# Revit family: d0088071_REVIT-TP
name_source: partatom
category: Mechanical Equipment
revit_build: Autodesk Revit 2017 (Build: 20190507_1515(x64)
units: mm (PartAtom-declared; Revit-internal decimal feet)

## family parameters
Always vertical = Yes
Cut with Voids When Loaded = No
Part Type = Normal
Room Calculation Point = No
Round Connector Dimension = Use Radius
Shared = No
Work Plane-Based = No

## types (58) — shared parameters
250 GT Visibility = No
3500 4000 GT Visibility = No
500 3000 GT Visibility = Yes
Aquaplex = Yes
Assembly Code = D3040400
Blower Motor HP = 0.33333
Description = PVI Turbopower - Water Heater
Disclaimer = This rendering is for building modeling purposes only. Submittal/catalog is still the contract document. PVI reserves the right to change design and specification without notice.
Drain Angle = 0.00°
Enclosure Height = 16"
Enclosure Width = 9"
Energy Radius = 14 1/2"
Flue Collector Radius = 11 1/4"
Flue Extension = 18 1/4"
Manufacturer = PVI Industries, LLC
Relief Valve NPT = 1"
Relief Valve Radius = 1/2"
URL = www.pvi.com

## per-type parameters (varying)
- 2500 L 1500 A-TP: 500-3000 GIY=5 7/8"; A=13 3/4"; Air Inlet Depth=7"; Air Inlet Diameter=8"; Air Inlet Extension=20 15/16"; Air Inlet Radius=4"; Air Inlet Width=9"; Air Inlet X=15 15/16"; Air Inlet Y=7 3/16"; Air Inlet Y Offset=2 11/16"; Air Inlet Z Offset=5 3/8"; B=4"; Burner Depth=25 15/16"; Burner Height=16 5/8"; Burner Width=22 1/4"; Clearance Front=114 1/2"; Clearance Rear=55 1/2"; Clearance Sides=55 1/2"; Cold Water Extension=38 1/2"; Cold Water NPT=3"; Cold Water Radius=1 1/2"; Control Panel Extension=44 1/2"; Current=2 A; Drain Extension=41 3/8"; Drain NPT=1 1/2"; Drain Radius=3/4"; Energy Extension=49 1/16"; FC OAL=64 9/16"; Flat Side Distance=75"; Flue Collector Extension=15 1/2"; Flue Diameter=10"; Flue Location=56 13/16"; Flue Radius=5"; Front Skid Extension=112 1/2"; GT Conn Z=104 15/16"; GT Z=66 9/16"; Gas Conn X=44 1/8"; Gas Conn Y=15 7/8"; Gas Inlet NPT=2 1/2"; Gas Inlet Radius=1 1/4"; Gas Inlet X=24 1/8"; Gas Inlet Y=5 7/8"; Gas Inlet Z=40 3/8"; Height to Cold Inlet=21 1/4"; Height to Drain=2 1/4"; Height to Energy=32 3/8"; Height to Hot Outlet=84 1/2"; Height to Hot Outlet Actual=84 1/2"; Height to Relief=85 1/8"; Height to Relief Actual=85 1/8"; Hot Outlet Angle=90.00°; Hot Water Extension=38 1/2"; Hot Water NPT=3"; Hot Water Radius=1 1/2"; Input Btu/h=2010000; Nominal Storage=1500 gal; Rear Access Extension=-45 1/2"; Rear Skid Extension=37 1/2"; Recovery Rate 40F to 140F (gph)=2000; Relief Extension=40 1/2"; Size=1500; Skid Center Dist=21 1/2"; Skid Length=75"; Skid Spacing=43"; Unit Height=104 1/2"; Unit Height Actual=104 1/2"; Unit Radius=37 1/2"; Weight=4540
- 2000 L 1500 A-TP: 500-3000 GIY=5 1/2"; A=13 3/4"; Air Inlet Depth=7"; Air Inlet Diameter=8"; Air Inlet Extension=20 15/16"; Air Inlet Radius=4"; Air Inlet Width=9"; Air Inlet X=15 15/16"; Air Inlet Y=7 3/16"; Air Inlet Y Offset=2 11/16"; Air Inlet Z Offset=5 3/8"; B=4"; Burner Depth=25 15/16"; Burner Height=16 5/8"; Burner Width=22 1/4"; Clearance Front=114 1/2"; Clearance Rear=55 1/2"; Clearance Sides=55 1/2"; Cold Water Extension=38 1/2"; Cold Water NPT=3"; Cold Water Radius=1 1/2"; Control Panel Extension=44 1/2"; Current=2 A; Drain Extension=41 3/8"; Drain NPT=1 1/2"; Drain Radius=3/4"; Energy Extension=49 1/16"; FC OAL=64 9/16"; Flat Side Distance=75"; Flue Collector Extension=15 1/2"; Flue Diameter=10"; Flue Location=56 13/16"; Flue Radius=5"; Front Skid Extension=112 1/2"; GT Conn Z=100 5/8"; GT Z=66 9/16"; Gas Conn X=42"; Gas Conn Y=15 1/2"; Gas Inlet NPT=2"; Gas Inlet Radius=1"; Gas Inlet X=22"; Gas Inlet Y=5 1/2"; Gas Inlet Z=36 1/16"; Height to Cold Inlet=21 1/4"; Height to Drain=2 1/4"; Height to Energy=32 3/8"; Height to Hot Outlet=84 1/2"; Height to Hot Outlet Actual=84 1/2"; Height to Relief=85 1/8"; Height to Relief Actual=85 1/8"; Hot Outlet Angle=90.00°; Hot Water Extension=38 1/2"; Hot Water NPT=3"; Hot Water Radius=1 1/2"; Input Btu/h=1600000; Nominal Storage=1500 gal; Rear Access Extension=-45 1/2"; Rear Skid Extension=37 1/2"; Recovery Rate 40F to 140F (gph)=1600; Relief Extension=40 1/2"; Size=1500; Skid Center Dist=21 1/2"; Skid Length=75"; Skid Spacing=43"; Unit Height=104 1/2"; Unit Height Actual=104 1/2"; Unit Radius=37 1/2"; Weight=4520
- 1500 L 1500 A-TP: 500-3000 GIY=5 1/2"; A=8 3/8"; Air Inlet Depth=3 1/8"; Air Inlet Diameter=6"; Air Inlet Extension=18 15/16"; Air Inlet Radius=3"; Air Inlet Width=6 3/8"; Air Inlet X=14 7/8"; Air Inlet Y=5 1/4"; Air Inlet Y Offset=2 1/16"; Air Inlet Z Offset=2 1/16"; B=3 15/16"; Burner Depth=15 1/2"; Burner Height=13 3/4"; Burner Width=14 11/16"; Clearance Front=99 1/2"; Clearance Rear=55 1/2"; Clearance Sides=55 1/2"; Cold Water Extension=38 1/2"; Cold Water NPT=3"; Cold Water Radius=1 1/2"; Control Panel Extension=44 1/2"; Current=2 A; Drain Extension=41 3/8"; Drain NPT=1 1/2"; Drain Radius=3/4"; Energy Extension=44 1/2"; FC OAL=60"; Flat Side Distance=75"; Flue Collector Extension=15 1/2"; Flue Diameter=8"; Flue Location=52 1/4"; Flue Radius=4"; Front Skid Extension=112 1/2"; GT Conn Z=96 7/16"; GT Z=62"; Gas Conn X=40 1/2"; Gas Conn Y=15 1/2"; Gas Inlet NPT=2"; Gas Inlet Radius=1"; Gas Inlet X=20 1/2"; Gas Inlet Y=5 1/2"; Gas Inlet Z=36 7/16"; Height to Cold Inlet=21 1/4"; Height to Drain=2 1/4"; Height to Energy=32 3/8"; Height to Hot Outlet=84 1/2"; Height to Hot Outlet Actual=84 1/2"; Height to Relief=85 1/8"; Height to Relief Actual=85 1/8"; Hot Outlet Angle=90.00°; Hot Water Extension=38 1/2"; Hot Water NPT=3"; Hot Water Radius=1 1/2"; Input Btu/h=1200000; Nominal Storage=1500 gal; Rear Access Extension=0"; Rear Skid Extension=37 1/2"; Recovery Rate 40F to 140F (gph)=1200; Relief Extension=40 1/2"; Size=1500; Skid Center Dist=21 1/2"; Skid Length=75"; Skid Spacing=43"; Unit Height=104 1/2"; Unit Height Actual=104 1/2"; Unit Radius=37 1/2"; Weight=4085
- 1250 L 1500 A-TP: 500-3000 GIY=5 1/2"; A=8 3/8"; Air Inlet Depth=3 1/8"; Air Inlet Diameter=6"; Air Inlet Extension=18 15/16"; Air Inlet Radius=3"; Air Inlet Width=6 3/8"; Air Inlet X=14 7/8"; Air Inlet Y=5 1/4"; Air Inlet Y Offset=2 1/16"; Air Inlet Z Offset=2 1/16"; B=3 15/16"; Burner Depth=15 1/2"; Burner Height=13 3/4"; Burner Width=14 11/16"; Clearance Front=99 1/2"; Clearance Rear=55 1/2"; Clearance Sides=55 1/2"; Cold Water Extension=38 1/2"; Cold Water NPT=3"; Cold Water Radius=1 1/2"; Control Panel Extension=44 1/2"; Current=2 A; Drain Extension=41 3/8"; Drain NPT=1 1/2"; Drain Radius=3/4"; Energy Extension=44 1/2"; FC OAL=60"; Flat Side Distance=75"; Flue Collector Extension=15 1/2"; Flue Diameter=8"; Flue Location=52 1/4"; Flue Radius=4"; Front Skid Extension=112 1/2"; GT Conn Z=96 7/16"; GT Z=62"; Gas Conn X=40 1/2"; Gas Conn Y=15 1/2"; Gas Inlet NPT=2"; Gas Inlet Radius=1"; Gas Inlet X=20 1/2"; Gas Inlet Y=5 1/2"; Gas Inlet Z=36 7/16"; Height to Cold Inlet=21 1/4"; Height to Drain=2 1/4"; Height to Energy=32 3/8"; Height to Hot Outlet=84 1/2"; Height to Hot Outlet Actual=84 1/2"; Height to Relief=85 1/8"; Height to Relief Actual=85 1/8"; Hot Outlet Angle=90.00°; Hot Water Extension=38 1/2"; Hot Water NPT=3"; Hot Water Radius=1 1/2"; Input Btu/h=1000000; Nominal Storage=1500 gal; Rear Access Extension=0"; Rear Skid Extension=37 1/2"; Recovery Rate 40F to 140F (gph)=1000; Relief Extension=40 1/2"; Size=1500; Skid Center Dist=21 1/2"; Skid Length=75"; Skid Spacing=43"; Unit Height=104 1/2"; Unit Height Actual=104 1/2"; Unit Radius=37 1/2"; Weight=4075
- 1000 L 1500 A-TP: 500-3000 GIY=4 1/2"; A=8 3/8"; Air Inlet Depth=3 1/8"; Air Inlet Diameter=6"; Air Inlet Extension=18 15/16"; Air Inlet Radius=3"; Air Inlet Width=6 3/8"; Air Inlet X=14 7/8"; Air Inlet Y=5 1/4"; Air Inlet Y Offset=2 1/16"; Air Inlet Z Offset=2 1/16"; B=3 15/16"; Burner Depth=15 1/2"; Burner Height=13 3/4"; Burner Width=14 11/16"; Clearance Front=91 1/2"; Clearance Rear=55 1/2"; Clearance Sides=55 1/2"; Cold Water Extension=38 1/2"; Cold Water NPT=3"; Cold Water Radius=1 1/2"; Control Panel Extension=44 1/2"; Current=2 A; Drain Extension=41 3/8"; Drain NPT=1 1/2"; Drain Radius=3/4"; Energy Extension=43 3/4"; FC OAL=52"; Flat Side Distance=75"; Flue Collector Extension=8 1/4"; Flue Diameter=8"; Flue Location=47 7/8"; Flue Radius=4"; Front Skid Extension=112 1/2"; GT Conn Z=79 11/16"; GT Z=54"; Gas Conn X=40 1/2"; Gas Conn Y=14 1/2"; Gas Inlet NPT=1 1/4"; Gas Inlet Radius=5/8"; Gas Inlet X=20 1/2"; Gas Inlet Y=4 1/2"; Gas Inlet Z=27 11/16"; Height to Cold Inlet=21 1/4"; Height to Drain=2 1/4"; Height to Energy=32 3/8"; Height to Hot Outlet=84 1/2"; Height to Hot Outlet Actual=84 1/2"; Height to Relief=85 1/8"; Height to Relief Actual=85 1/8"; Hot Outlet Angle=90.00°; Hot Water Extension=38 1/2"; Hot Water NPT=3"; Hot Water Radius=1 1/2"; Input Btu/h=800000; Nominal Storage=1500 gal; Rear Access Extension=0"; Rear Skid Extension=37 1/2"; Recovery Rate 40F to 140F (gph)=800; Relief Extension=40 1/2"; Size=1500; Skid Center Dist=21 1/2"; Skid Length=75"; Skid Spacing=43"; Unit Height=104 1/2"; Unit Height Actual=104 1/2"; Unit Radius=37 1/2"; Weight=3805
- 750 L 1500 A-TP: 500-3000 GIY=3 5/8"; A=8 3/8"; Air Inlet Depth=3 1/8"; Air Inlet Diameter=6"; Air Inlet Extension=18 15/16"; Air Inlet Radius=3"; Air Inlet Width=6 3/8"; Air Inlet X=14 7/8"; Air Inlet Y=5 1/4"; Air Inlet Y Offset=2 1/16"; Air Inlet Z Offset=2 1/16"; B=3 15/16"; Burner Depth=15 1/2"; Burner Height=13 3/4"; Burner Width=14 11/16"; Clearance Front=91 1/2"; Clearance Rear=55 1/2"; Clearance Sides=55 1/2"; Cold Water Extension=38 1/2"; Cold Water NPT=3"; Cold Water Radius=1 1/2"; Control Panel Extension=44 1/2"; Current=2 A; Drain Extension=41 3/8"; Drain NPT=1 1/2"; Drain Radius=3/4"; Energy Extension=43 3/4"; FC OAL=52"; Flat Side Distance=75"; Flue Collector Extension=8 1/4"; Flue Diameter=6"; Flue Location=47 7/8"; Flue Radius=3"; Front Skid Extension=112 1/2"; GT Conn Z=74 5/8"; GT Z=54"; Gas Conn X=36 7/8"; Gas Conn Y=13 5/8"; Gas Inlet NPT=1"; Gas Inlet Radius=1/2"; Gas Inlet X=16 7/8"; Gas Inlet Y=3 5/8"; Gas Inlet Z=22 5/8"; Height to Cold Inlet=21 1/4"; Height to Drain=2 1/4"; Height to Energy=32 3/8"; Height to Hot Outlet=84 1/2"; Height to Hot Outlet Actual=84 1/2"; Height to Relief=85 1/8"; Height to Relief Actual=85 1/8"; Hot Outlet Angle=90.00°; Hot Water Extension=38 1/2"; Hot Water NPT=3"; Hot Water Radius=1 1/2"; Input Btu/h=600000; Nominal Storage=1500 gal; Rear Access Extension=0"; Rear Skid Extension=37 1/2"; Recovery Rate 40F to 140F (gph)=600; Relief Extension=40 1/2"; Size=1500; Skid Center Dist=21 1/2"; Skid Length=75"; Skid Spacing=43"; Unit Height=104 1/2"; Unit Height Actual=104 1/2"; Unit Radius=37 1/2"; Weight=3765
- 2500 L 1250 A-TP: 500-3000 GIY=5 7/8"; A=13 3/4"; Air Inlet Depth=7"; Air Inlet Diameter=8"; Air Inlet Extension=20 15/16"; Air Inlet Radius=4"; Air Inlet Width=9"; Air Inlet X=15 15/16"; Air Inlet Y=7 3/16"; Air Inlet Y Offset=2 11/16"; Air Inlet Z Offset=5 3/8"; B=4"; Burner Depth=25 15/16"; Burner Height=16 5/8"; Burner Width=22 1/4"; Clearance Front=114 1/2"; Clearance Rear=55 1/2"; Clearance Sides=55 1/2"; Cold Water Extension=38 1/2"; Cold Water NPT=3"; Cold Water Radius=1 1/2"; Control Panel Extension=44 1/2"; Current=2 A; Drain Extension=41 3/8"; Drain NPT=1 1/2"; Drain Radius=3/4"; Energy Extension=49 1/16"; FC OAL=64 9/16"; Flat Side Distance=75"; Flue Collector Extension=15 1/2"; Flue Diameter=10"; Flue Location=56 13/16"; Flue Radius=5"; Front Skid Extension=112 1/2"; GT Conn Z=104 15/16"; GT Z=66 9/16"; Gas Conn X=44 1/8"; Gas Conn Y=15 7/8"; Gas Inlet NPT=2 1/2"; Gas Inlet Radius=1 1/4"; Gas Inlet X=24 1/8"; Gas Inlet Y=5 7/8"; Gas Inlet Z=40 3/8"; Height to Cold Inlet=21 1/4"; Height to Drain=2 1/4"; Height to Energy=32 3/8"; Height to Hot Outlet=72 1/2"; Height to Hot Outlet Actual=72 1/2"; Height to Relief=73 1/8"; Height to Relief Actual=73 1/8"; Hot Outlet Angle=90.00°; Hot Water Extension=38 1/2"; Hot Water NPT=3"; Hot Water Radius=1 1/2"; Input Btu/h=2010000; Nominal Storage=1250 gal; Rear Access Extension=-45 1/2"; Rear Skid Extension=37 1/2"; Recovery Rate 40F to 140F (gph)=2000; Relief Extension=40 1/2"; Size=1250; Skid Center Dist=21 1/2"; Skid Length=75"; Skid Spacing=43"; Unit Height=92 1/2"; Unit Height Actual=92 1/2"; Unit Radius=37 1/2"; Weight=4325
- 2000 L 1250 A-TP: 500-3000 GIY=5 1/2"; A=13 3/4"; Air Inlet Depth=7"; Air Inlet Diameter=8"; Air Inlet Extension=20 15/16"; Air Inlet Radius=4"; Air Inlet Width=9"; Air Inlet X=15 15/16"; Air Inlet Y=7 3/16"; Air Inlet Y Offset=2 11/16"; Air Inlet Z Offset=5 3/8"; B=4"; Burner Depth=25 15/16"; Burner Height=16 5/8"; Burner Width=22 1/4"; Clearance Front=114 1/2"; Clearance Rear=55 1/2"; Clearance Sides=55 1/2"; Cold Water Extension=38 1/2"; Cold Water NPT=3"; Cold Water Radius=1 1/2"; Control Panel Extension=44 1/2"; Current=2 A; Drain Extension=41 3/8"; Drain NPT=1 1/2"; Drain Radius=3/4"; Energy Extension=49 1/16"; FC OAL=64 9/16"; Flat Side Distance=75"; Flue Collector Extension=15 1/2"; Flue Diameter=10"; Flue Location=56 13/16"; Flue Radius=5"; Front Skid Extension=112 1/2"; GT Conn Z=100 5/8"; GT Z=66 9/16"; Gas Conn X=42"; Gas Conn Y=15 1/2"; Gas Inlet NPT=2"; Gas Inlet Radius=1"; Gas Inlet X=22"; Gas Inlet Y=5 1/2"; Gas Inlet Z=36 1/16"; Height to Cold Inlet=21 1/4"; Height to Drain=2 1/4"; Height to Energy=32 3/8"; Height to Hot Outlet=72 1/2"; Height to Hot Outlet Actual=72 1/2"; Height to Relief=73 1/8"; Height to Relief Actual=73 1/8"; Hot Outlet Angle=90.00°; Hot Water Extension=38 1/2"; Hot Water NPT=3"; Hot Water Radius=1 1/2"; Input Btu/h=1600000; Nominal Storage=1250 gal; Rear Access Extension=-45 1/2"; Rear Skid Extension=37 1/2"; Recovery Rate 40F to 140F (gph)=1600; Relief Extension=40 1/2"; Size=1250; Skid Center Dist=21 1/2"; Skid Length=75"; Skid Spacing=43"; Unit Height=92 1/2"; Unit Height Actual=92 1/2"; Unit Radius=37 1/2"; Weight=4305
- 1500 L 1250 A-TP: 500-3000 GIY=5 1/2"; A=8 3/8"; Air Inlet Depth=3 1/8"; Air Inlet Diameter=6"; Air Inlet Extension=18 15/16"; Air Inlet Radius=3"; Air Inlet Width=6 3/8"; Air Inlet X=14 7/8"; Air Inlet Y=5 1/4"; Air Inlet Y Offset=2 1/16"; Air Inlet Z Offset=2 1/16"; B=3 15/16"; Burner Depth=15 1/2"; Burner Height=13 3/4"; Burner Width=14 11/16"; Clearance Front=99 1/2"; Clearance Rear=55 1/2"; Clearance Sides=55 1/2"; Cold Water Extension=38 1/2"; Cold Water NPT=3"; Cold Water Radius=1 1/2"; Control Panel Extension=44 1/2"; Current=2 A; Drain Extension=41 3/8"; Drain NPT=1 1/2"; Drain Radius=3/4"; Energy Extension=44 1/2"; FC OAL=60"; Flat Side Distance=75"; Flue Collector Extension=15 1/2"; Flue Diameter=8"; Flue Location=52 1/4"; Flue Radius=4"; Front Skid Extension=112 1/2"; GT Conn Z=96 7/16"; GT Z=62"; Gas Conn X=40 1/2"; Gas Conn Y=15 1/2"; Gas Inlet NPT=2"; Gas Inlet Radius=1"; Gas Inlet X=20 1/2"; Gas Inlet Y=5 1/2"; Gas Inlet Z=36 7/16"; Height to Cold Inlet=21 1/4"; Height to Drain=2 1/4"; Height to Energy=32 3/8"; Height to Hot Outlet=72 1/2"; Height to Hot Outlet Actual=72 1/2"; Height to Relief=73 1/8"; Height to Relief Actual=73 1/8"; Hot Outlet Angle=90.00°; Hot Water Extension=38 1/2"; Hot Water NPT=3"; Hot Water Radius=1 1/2"; Input Btu/h=1200000; Nominal Storage=1250 gal; Rear Access Extension=0"; Rear Skid Extension=37 1/2"; Recovery Rate 40F to 140F (gph)=1200; Relief Extension=40 1/2"; Size=1250; Skid Center Dist=21 1/2"; Skid Length=75"; Skid Spacing=43"; Unit Height=92 1/2"; Unit Height Actual=92 1/2"; Unit Radius=37 1/2"; Weight=3870
- 1250 L 1250 A-TP: 500-3000 GIY=5 1/2"; A=8 3/8"; Air Inlet Depth=3 1/8"; Air Inlet Diameter=6"; Air Inlet Extension=18 15/16"; Air Inlet Radius=3"; Air Inlet Width=6 3/8"; Air Inlet X=14 7/8"; Air Inlet Y=5 1/4"; Air Inlet Y Offset=2 1/16"; Air Inlet Z Offset=2 1/16"; B=3 15/16"; Burner Depth=15 1/2"; Burner Height=13 3/4"; Burner Width=14 11/16"; Clearance Front=99 1/2"; Clearance Rear=55 1/2"; Clearance Sides=55 1/2"; Cold Water Extension=38 1/2"; Cold Water NPT=3"; Cold Water Radius=1 1/2"; Control Panel Extension=44 1/2"; Current=2 A; Drain Extension=41 3/8"; Drain NPT=1 1/2"; Drain Radius=3/4"; Energy Extension=44 1/2"; FC OAL=60"; Flat Side Distance=75"; Flue Collector Extension=15 1/2"; Flue Diameter=8"; Flue Location=52 1/4"; Flue Radius=4"; Front Skid Extension=112 1/2"; GT Conn Z=96 7/16"; GT Z=62"; Gas Conn X=40 1/2"; Gas Conn Y=15 1/2"; Gas Inlet NPT=2"; Gas Inlet Radius=1"; Gas Inlet X=20 1/2"; Gas Inlet Y=5 1/2"; Gas Inlet Z=36 7/16"; Height to Cold Inlet=21 1/4"; Height to Drain=2 1/4"; Height to Energy=32 3/8"; Height to Hot Outlet=72 1/2"; Height to Hot Outlet Actual=72 1/2"; Height to Relief=73 1/8"; Height to Relief Actual=73 1/8"; Hot Outlet Angle=90.00°; Hot Water Extension=38 1/2"; Hot Water NPT=3"; Hot Water Radius=1 1/2"; Input Btu/h=1000000; Nominal Storage=1250 gal; Rear Access Extension=0"; Rear Skid Extension=37 1/2"; Recovery Rate 40F to 140F (gph)=1000; Relief Extension=40 1/2"; Size=1250; Skid Center Dist=21 1/2"; Skid Length=75"; Skid Spacing=43"; Unit Height=92 1/2"; Unit Height Actual=92 1/2"; Unit Radius=37 1/2"; Weight=3860
- 1000 L 1250 A-TP: 500-3000 GIY=4 1/2"; A=8 3/8"; Air Inlet Depth=3 1/8"; Air Inlet Diameter=6"; Air Inlet Extension=18 15/16"; Air Inlet Radius=3"; Air Inlet Width=6 3/8"; Air Inlet X=14 7/8"; Air Inlet Y=5 1/4"; Air Inlet Y Offset=2 1/16"; Air Inlet Z Offset=2 1/16"; B=3 15/16"; Burner Depth=15 1/2"; Burner Height=13 3/4"; Burner Width=14 11/16"; Clearance Front=91 1/2"; Clearance Rear=55 1/2"; Clearance Sides=55 1/2"; Cold Water Extension=38 1/2"; Cold Water NPT=3"; Cold Water Radius=1 1/2"; Control Panel Extension=44 1/2"; Current=2 A; Drain Extension=41 3/8"; Drain NPT=1 1/2"; Drain Radius=3/4"; Energy Extension=43 3/4"; FC OAL=52"; Flat Side Distance=75"; Flue Collector Extension=8 1/4"; Flue Diameter=8"; Flue Location=47 7/8"; Flue Radius=4"; Front Skid Extension=112 1/2"; GT Conn Z=79 11/16"; GT Z=54"; Gas Conn X=40 1/2"; Gas Conn Y=14 1/2"; Gas Inlet NPT=1 1/4"; Gas Inlet Radius=5/8"; Gas Inlet X=20 1/2"; Gas Inlet Y=4 1/2"; Gas Inlet Z=27 11/16"; Height to Cold Inlet=21 1/4"; Height to Drain=2 1/4"; Height to Energy=32 3/8"; Height to Hot Outlet=72 1/2"; Height to Hot Outlet Actual=72 1/2"; Height to Relief=73 1/8"; Height to Relief Actual=73 1/8"; Hot Outlet Angle=90.00°; Hot Water Extension=38 1/2"; Hot Water NPT=3"; Hot Water Radius=1 1/2"; Input Btu/h=800000; Nominal Storage=1250 gal; Rear Access Extension=0"; Rear Skid Extension=37 1/2"; Recovery Rate 40F to 140F (gph)=800; Relief Extension=40 1/2"; Size=1250; Skid Center Dist=21 1/2"; Skid Length=75"; Skid Spacing=43"; Unit Height=92 1/2"; Unit Height Actual=92 1/2"; Unit Radius=37 1/2"; Weight=3590
- 750 L 1250 A-TP: 500-3000 GIY=3 5/8"; A=8 3/8"; Air Inlet Depth=3 1/8"; Air Inlet Diameter=6"; Air Inlet Extension=18 15/16"; Air Inlet Radius=3"; Air Inlet Width=6 3/8"; Air Inlet X=14 7/8"; Air Inlet Y=5 1/4"; Air Inlet Y Offset=2 1/16"; Air Inlet Z Offset=2 1/16"; B=3 15/16"; Burner Depth=15 1/2"; Burner Height=13 3/4"; Burner Width=14 11/16"; Clearance Front=91 1/2"; Clearance Rear=55 1/2"; Clearance Sides=55 1/2"; Cold Water Extension=38 1/2"; Cold Water NPT=3"; Cold Water Radius=1 1/2"; Control Panel Extension=44 1/2"; Current=2 A; Drain Extension=41 3/8"; Drain NPT=1 1/2"; Drain Radius=3/4"; Energy Extension=43 3/4"; FC OAL=52"; Flat Side Distance=75"; Flue Collector Extension=8 1/4"; Flue Diameter=6"; Flue Location=47 7/8"; Flue Radius=3"; Front Skid Extension=112 1/2"; GT Conn Z=74 5/8"; GT Z=54"; Gas Conn X=36 7/8"; Gas Conn Y=13 5/8"; Gas Inlet NPT=1"; Gas Inlet Radius=1/2"; Gas Inlet X=16 7/8"; Gas Inlet Y=3 5/8"; Gas Inlet Z=22 5/8"; Height to Cold Inlet=21 1/4"; Height to Drain=2 1/4"; Height to Energy=32 3/8"; Height to Hot Outlet=72 1/2"; Height to Hot Outlet Actual=72 1/2"; Height to Relief=73 1/8"; Height to Relief Actual=73 1/8"; Hot Outlet Angle=90.00°; Hot Water Extension=38 1/2"; Hot Water NPT=3"; Hot Water Radius=1 1/2"; Input Btu/h=600000; Nominal Storage=1250 gal; Rear Access Extension=0"; Rear Skid Extension=37 1/2"; Recovery Rate 40F to 140F (gph)=600; Relief Extension=40 1/2"; Size=1250; Skid Center Dist=21 1/2"; Skid Length=75"; Skid Spacing=43"; Unit Height=92 1/2"; Unit Height Actual=92 1/2"; Unit Radius=37 1/2"; Weight=3550
- 2500 L 900 A-TP: 500-3000 GIY=5 7/8"; A=13 3/4"; Air Inlet Depth=7"; Air Inlet Diameter=8"; Air Inlet Extension=20 15/16"; Air Inlet Radius=4"; Air Inlet Width=9"; Air Inlet X=15 15/16"; Air Inlet Y=7 3/16"; Air Inlet Y Offset=2 11/16"; Air Inlet Z Offset=5 3/8"; B=4"; Burner Depth=25 15/16"; Burner Height=16 5/8"; Burner Width=22 1/4"; Clearance Front=109"; Clearance Rear=51 1/4"; Clearance Sides=51 1/4"; Cold Water Extension=34 1/4"; Cold Water NPT=3"; Cold Water Radius=1 1/2"; Control Panel Extension=40 1/4"; Current=2 A; Drain Extension=37 1/8"; Drain NPT=1 1/2"; Drain Radius=3/4"; Energy Extension=43 9/16"; FC OAL=59 1/16"; Flat Side Distance=66 1/2"; Flue Collector Extension=15 1/2"; Flue Diameter=10"; Flue Location=51 5/16"; Flue Radius=5"; Front Skid Extension=100 1/4"; GT Conn Z=99 7/16"; GT Z=61 1/16"; Gas Conn X=44 1/8"; Gas Conn Y=15 7/8"; Gas Inlet NPT=2 1/2"; Gas Inlet Radius=1 1/4"; Gas Inlet X=24 1/8"; Gas Inlet Y=5 7/8"; Gas Inlet Z=40 3/8"; Height to Cold Inlet=21 1/4"; Height to Drain=2 1/4"; Height to Energy=32 5/8"; Height to Hot Outlet=72 7/8"; Height to Hot Outlet Actual=72 7/8"; Height to Relief=73 1/2"; Height to Relief Actual=73 1/2"; Hot Outlet Angle=90.00°; Hot Water Extension=34 1/4"; Hot Water NPT=3"; Hot Water Radius=1 1/2"; Input Btu/h=2010000; Nominal Storage=900 gal; Rear Access Extension=-41 1/4"; Rear Skid Extension=33 1/4"; Recovery Rate 40F to 140F (gph)=2000; Relief Extension=36 1/4"; Size=900; Skid Center Dist=18"; Skid Length=67"; Skid Spacing=36"; Unit Height=93 1/2"; Unit Height Actual=93 1/2"; Unit Radius=33 1/4"; Weight=3280
- 2000 L 900 A-TP: 500-3000 GIY=5 1/2"; A=13 3/4"; Air Inlet Depth=7"; Air Inlet Diameter=8"; Air Inlet Extension=20 15/16"; Air Inlet Radius=4"; Air Inlet Width=9"; Air Inlet X=15 15/16"; Air Inlet Y=7 3/16"; Air Inlet Y Offset=2 11/16"; Air Inlet Z Offset=5 3/8"; B=4"; Burner Depth=25 15/16"; Burner Height=16 5/8"; Burner Width=22 1/4"; Clearance Front=109"; Clearance Rear=51 1/4"; Clearance Sides=51 1/4"; Cold Water Extension=34 1/4"; Cold Water NPT=3"; Cold Water Radius=1 1/2"; Control Panel Extension=40 1/4"; Current=2 A; Drain Extension=37 1/8"; Drain NPT=1 1/2"; Drain Radius=3/4"; Energy Extension=43 9/16"; FC OAL=59 1/16"; Flat Side Distance=66 1/2"; Flue Collector Extension=15 1/2"; Flue Diameter=10"; Flue Location=51 5/16"; Flue Radius=5"; Front Skid Extension=100 1/4"; GT Conn Z=95 1/8"; GT Z=61 1/16"; Gas Conn X=42"; Gas Conn Y=15 1/2"; Gas Inlet NPT=2"; Gas Inlet Radius=1"; Gas Inlet X=22"; Gas Inlet Y=5 1/2"; Gas Inlet Z=36 1/16"; Height to Cold Inlet=21 1/4"; Height to Drain=2 1/4"; Height to Energy=32 5/8"; Height to Hot Outlet=72 7/8"; Height to Hot Outlet Actual=72 7/8"; Height to Relief=73 1/2"; Height to Relief Actual=73 1/2"; Hot Outlet Angle=90.00°; Hot Water Extension=34 1/4"; Hot Water NPT=3"; Hot Water Radius=1 1/2"; Input Btu/h=1600000; Nominal Storage=900 gal; Rear Access Extension=-41 1/4"; Rear Skid Extension=33 1/4"; Recovery Rate 40F to 140F (gph)=1600; Relief Extension=36 1/4"; Size=900; Skid Center Dist=18"; Skid Length=67"; Skid Spacing=36"; Unit Height=93 1/2"; Unit Height Actual=93 1/2"; Unit Radius=33 1/4"; Weight=3260
- 1500 L 900 A-TP: 500-3000 GIY=5 1/2"; A=8 3/8"; Air Inlet Depth=3 1/8"; Air Inlet Diameter=6"; Air Inlet Extension=18 15/16"; Air Inlet Radius=3"; Air Inlet Width=6 3/8"; Air Inlet X=14 7/8"; Air Inlet Y=5 1/4"; Air Inlet Y Offset=2 1/16"; Air Inlet Z Offset=2 1/16"; B=3 15/16"; Burner Depth=15 1/2"; Burner Height=13 3/4"; Burner Width=14 11/16"; Clearance Front=94"; Clearance Rear=51 1/4"; Clearance Sides=51 1/4"; Cold Water Extension=34 1/4"; Cold Water NPT=3"; Cold Water Radius=1 1/2"; Control Panel Extension=40 1/4"; Current=2 A; Drain Extension=37 1/8"; Drain NPT=1 1/2"; Drain Radius=3/4"; Energy Extension=39"; FC OAL=54 1/2"; Flat Side Distance=66 1/2"; Flue Collector Extension=15 1/2"; Flue Diameter=8"; Flue Location=46 3/4"; Flue Radius=4"; Front Skid Extension=100 1/4"; GT Conn Z=90 15/16"; GT Z=56 1/2"; Gas Conn X=40 1/2"; Gas Conn Y=15 1/2"; Gas Inlet NPT=2"; Gas Inlet Radius=1"; Gas Inlet X=20 1/2"; Gas Inlet Y=5 1/2"; Gas Inlet Z=36 7/16"; Height to Cold Inlet=21 1/4"; Height to Drain=2 1/4"; Height to Energy=32 5/8"; Height to Hot Outlet=72 7/8"; Height to Hot Outlet Actual=72 7/8"; Height to Relief=73 1/2"; Height to Relief Actual=73 1/2"; Hot Outlet Angle=90.00°; Hot Water Extension=34 1/4"; Hot Water NPT=3"; Hot Water Radius=1 1/2"; Input Btu/h=1200000; Nominal Storage=900 gal; Rear Access Extension=0"; Rear Skid Extension=33 1/4"; Recovery Rate 40F to 140F (gph)=1200; Relief Extension=36 1/4"; Size=900; Skid Center Dist=18"; Skid Length=67"; Skid Spacing=36"; Unit Height=93 1/2"; Unit Height Actual=93 1/2"; Unit Radius=33 1/4"; Weight=2990
- 1250 L 900 A-TP: 500-3000 GIY=5 1/2"; A=8 3/8"; Air Inlet Depth=3 1/8"; Air Inlet Diameter=6"; Air Inlet Extension=18 15/16"; Air Inlet Radius=3"; Air Inlet Width=6 3/8"; Air Inlet X=14 7/8"; Air Inlet Y=5 1/4"; Air Inlet Y Offset=2 1/16"; Air Inlet Z Offset=2 1/16"; B=3 15/16"; Burner Depth=15 1/2"; Burner Height=13 3/4"; Burner Width=14 11/16"; Clearance Front=94"; Clearance Rear=51 1/4"; Clearance Sides=51 1/4"; Cold Water Extension=34 1/4"; Cold Water NPT=3"; Cold Water Radius=1 1/2"; Control Panel Extension=40 1/4"; Current=2 A; Drain Extension=37 1/8"; Drain NPT=1 1/2"; Drain Radius=3/4"; Energy Extension=39"; FC OAL=54 1/2"; Flat Side Distance=66 1/2"; Flue Collector Extension=15 1/2"; Flue Diameter=8"; Flue Location=46 3/4"; Flue Radius=4"; Front Skid Extension=100 1/4"; GT Conn Z=90 15/16"; GT Z=56 1/2"; Gas Conn X=40 1/2"; Gas Conn Y=15 1/2"; Gas Inlet NPT=2"; Gas Inlet Radius=1"; Gas Inlet X=20 1/2"; Gas Inlet Y=5 1/2"; Gas Inlet Z=36 7/16"; Height to Cold Inlet=21 1/4"; Height to Drain=2 1/4"; Height to Energy=32 5/8"; Height to Hot Outlet=72 7/8"; Height to Hot Outlet Actual=72 7/8"; Height to Relief=73 1/2"; Height to Relief Actual=73 1/2"; Hot Outlet Angle=90.00°; Hot Water Extension=34 1/4"; Hot Water NPT=3"; Hot Water Radius=1 1/2"; Input Btu/h=1000000; Nominal Storage=900 gal; Rear Access Extension=0"; Rear Skid Extension=33 1/4"; Recovery Rate 40F to 140F (gph)=1000; Relief Extension=36 1/4"; Size=900; Skid Center Dist=18"; Skid Length=67"; Skid Spacing=36"; Unit Height=93 1/2"; Unit Height Actual=93 1/2"; Unit Radius=33 1/4"; Weight=2810
- 1000 L 900 A-TP: 500-3000 GIY=4 1/2"; A=8 3/8"; Air Inlet Depth=3 1/8"; Air Inlet Diameter=6"; Air Inlet Extension=18 15/16"; Air Inlet Radius=3"; Air Inlet Width=6 3/8"; Air Inlet X=14 7/8"; Air Inlet Y=5 1/4"; Air Inlet Y Offset=2 1/16"; Air Inlet Z Offset=2 1/16"; B=3 15/16"; Burner Depth=15 1/2"; Burner Height=13 3/4"; Burner Width=14 11/16"; Clearance Front=86"; Clearance Rear=51 1/4"; Clearance Sides=51 1/4"; Cold Water Extension=34 1/4"; Cold Water NPT=3"; Cold Water Radius=1 1/2"; Control Panel Extension=40 1/4"; Current=2 A; Drain Extension=37 1/8"; Drain NPT=1 1/2"; Drain Radius=3/4"; Energy Extension=38 1/4"; FC OAL=46 1/2"; Flat Side Distance=66 1/2"; Flue Collector Extension=8 1/4"; Flue Diameter=8"; Flue Location=42 3/8"; Flue Radius=4"; Front Skid Extension=100 1/4"; GT Conn Z=74 3/16"; GT Z=48 1/2"; Gas Conn X=40 1/2"; Gas Conn Y=14 1/2"; Gas Inlet NPT=1 1/4"; Gas Inlet Radius=5/8"; Gas Inlet X=20 1/2"; Gas Inlet Y=4 1/2"; Gas Inlet Z=27 11/16"; Height to Cold Inlet=21 1/4"; Height to Drain=2 1/4"; Height to Energy=32 5/8"; Height to Hot Outlet=72 7/8"; Height to Hot Outlet Actual=72 7/8"; Height to Relief=73 1/2"; Height to Relief Actual=73 1/2"; Hot Outlet Angle=90.00°; Hot Water Extension=34 1/4"; Hot Water NPT=3"; Hot Water Radius=1 1/2"; Input Btu/h=800000; Nominal Storage=900 gal; Rear Access Extension=0"; Rear Skid Extension=33 1/4"; Recovery Rate 40F to 140F (gph)=800; Relief Extension=36 1/4"; Size=900; Skid Center Dist=18"; Skid Length=67"; Skid Spacing=36"; Unit Height=93 1/2"; Unit Height Actual=93 1/2"; Unit Radius=33 1/4"; Weight=2540
- 750 L 900 A-TP: 500-3000 GIY=3 5/8"; A=8 3/8"; Air Inlet Depth=3 1/8"; Air Inlet Diameter=6"; Air Inlet Extension=18 15/16"; Air Inlet Radius=3"; Air Inlet Width=6 3/8"; Air Inlet X=14 7/8"; Air Inlet Y=5 1/4"; Air Inlet Y Offset=2 1/16"; Air Inlet Z Offset=2 1/16"; B=3 15/16"; Burner Depth=15 1/2"; Burner Height=13 3/4"; Burner Width=14 11/16"; Clearance Front=86"; Clearance Rear=51 1/4"; Clearance Sides=51 1/4"; Cold Water Extension=34 1/4"; Cold Water NPT=3"; Cold Water Radius=1 1/2"; Control Panel Extension=40 1/4"; Current=2 A; Drain Extension=37 1/8"; Drain NPT=1 1/2"; Drain Radius=3/4"; Energy Extension=38 1/4"; FC OAL=46 1/2"; Flat Side Distance=66 1/2"; Flue Collector Extension=8 1/4"; Flue Diameter=6"; Flue Location=42 3/8"; Flue Radius=3"; Front Skid Extension=100 1/4"; GT Conn Z=69 1/8"; GT Z=48 1/2"; Gas Conn X=36 7/8"; Gas Conn Y=13 5/8"; Gas Inlet NPT=1"; Gas Inlet Radius=1/2"; Gas Inlet X=16 7/8"; Gas Inlet Y=3 5/8"; Gas Inlet Z=22 5/8"; Height to Cold Inlet=21 1/4"; Height to Drain=2 1/4"; Height to Energy=32 5/8"; Height to Hot Outlet=72 7/8"; Height to Hot Outlet Actual=72 7/8"; Height to Relief=73 1/2"; Height to Relief Actual=73 1/2"; Hot Outlet Angle=90.00°; Hot Water Extension=34 1/4"; Hot Water NPT=3"; Hot Water Radius=1 1/2"; Input Btu/h=600000; Nominal Storage=900 gal; Rear Access Extension=0"; Rear Skid Extension=33 1/4"; Recovery Rate 40F to 140F (gph)=600; Relief Extension=36 1/4"; Size=900; Skid Center Dist=18"; Skid Length=67"; Skid Spacing=36"; Unit Height=93 1/2"; Unit Height Actual=93 1/2"; Unit Radius=33 1/4"; Weight=2500
- 2500 L 750 A-TP: 500-3000 GIY=5 7/8"; A=13 3/4"; Air Inlet Depth=7"; Air Inlet Diameter=8"; Air Inlet Extension=20 15/16"; Air Inlet Radius=4"; Air Inlet Width=9"; Air Inlet X=15 15/16"; Air Inlet Y=7 3/16"; Air Inlet Y Offset=2 11/16"; Air Inlet Z Offset=5 3/8"; B=4"; Burner Depth=25 15/16"; Burner Height=16 5/8"; Burner Width=22 1/4"; Clearance Front=109"; Clearance Rear=51 1/4"; Clearance Sides=51 1/4"; Cold Water Extension=34 1/4"; Cold Water NPT=3"; Cold Water Radius=1 1/2"; Control Panel Extension=40 1/4"; Current=2 A; Drain Extension=37 1/8"; Drain NPT=1 1/2"; Drain Radius=3/4"; Energy Extension=43 9/16"; FC OAL=59 1/16"; Flat Side Distance=66 1/2"; Flue Collector Extension=15 1/2"; Flue Diameter=10"; Flue Location=51 5/16"; Flue Radius=5"; Front Skid Extension=100 1/4"; GT Conn Z=99 7/16"; GT Z=61 1/16"; Gas Conn X=44 1/8"; Gas Conn Y=15 7/8"; Gas Inlet NPT=2 1/2"; Gas Inlet Radius=1 1/4"; Gas Inlet X=24 1/8"; Gas Inlet Y=5 7/8"; Gas Inlet Z=40 3/8"; Height to Cold Inlet=21 1/4"; Height to Drain=2 1/4"; Height to Energy=32 5/8"; Height to Hot Outlet=60 7/8"; Height to Hot Outlet Actual=60 7/8"; Height to Relief=61 1/2"; Height to Relief Actual=61 1/2"; Hot Outlet Angle=90.00°; Hot Water Extension=34 1/4"; Hot Water NPT=3"; Hot Water Radius=1 1/2"; Input Btu/h=2010000; Nominal Storage=750 gal; Rear Access Extension=-41 1/4"; Rear Skid Extension=33 1/4"; Recovery Rate 40F to 140F (gph)=2000; Relief Extension=36 1/4"; Size=750; Skid Center Dist=18"; Skid Length=67"; Skid Spacing=36"; Unit Height=81 1/2"; Unit Height Actual=81 1/2"; Unit Radius=33 1/4"; Weight=3055
- 2000 L 750 A-TP: 500-3000 GIY=5 1/2"; A=13 3/4"; Air Inlet Depth=7"; Air Inlet Diameter=8"; Air Inlet Extension=20 15/16"; Air Inlet Radius=4"; Air Inlet Width=9"; Air Inlet X=15 15/16"; Air Inlet Y=7 3/16"; Air Inlet Y Offset=2 11/16"; Air Inlet Z Offset=5 3/8"; B=4"; Burner Depth=25 15/16"; Burner Height=16 5/8"; Burner Width=22 1/4"; Clearance Front=109"; Clearance Rear=51 1/4"; Clearance Sides=51 1/4"; Cold Water Extension=34 1/4"; Cold Water NPT=3"; Cold Water Radius=1 1/2"; Control Panel Extension=40 1/4"; Current=2 A; Drain Extension=37 1/8"; Drain NPT=1 1/2"; Drain Radius=3/4"; Energy Extension=43 9/16"; FC OAL=59 1/16"; Flat Side Distance=66 1/2"; Flue Collector Extension=15 1/2"; Flue Diameter=10"; Flue Location=51 5/16"; Flue Radius=5"; Front Skid Extension=100 1/4"; GT Conn Z=95 1/8"; GT Z=61 1/16"; Gas Conn X=42"; Gas Conn Y=15 1/2"; Gas Inlet NPT=2"; Gas Inlet Radius=1"; Gas Inlet X=22"; Gas Inlet Y=5 1/2"; Gas Inlet Z=36 1/16"; Height to Cold Inlet=21 1/4"; Height to Drain=2 1/4"; Height to Energy=32 5/8"; Height to Hot Outlet=60 7/8"; Height to Hot Outlet Actual=60 7/8"; Height to Relief=61 1/2"; Height to Relief Actual=61 1/2"; Hot Outlet Angle=90.00°; Hot Water Extension=34 1/4"; Hot Water NPT=3"; Hot Water Radius=1 1/2"; Input Btu/h=1600000; Nominal Storage=750 gal; Rear Access Extension=-41 1/4"; Rear Skid Extension=33 1/4"; Recovery Rate 40F to 140F (gph)=1600; Relief Extension=36 1/4"; Size=750; Skid Center Dist=18"; Skid Length=67"; Skid Spacing=36"; Unit Height=81 1/2"; Unit Height Actual=81 1/2"; Unit Radius=33 1/4"; Weight=3035
- 1500 L 750 A-TP: 500-3000 GIY=5 1/2"; A=8 3/8"; Air Inlet Depth=3 1/8"; Air Inlet Diameter=6"; Air Inlet Extension=18 15/16"; Air Inlet Radius=3"; Air Inlet Width=6 3/8"; Air Inlet X=14 7/8"; Air Inlet Y=5 1/4"; Air Inlet Y Offset=2 1/16"; Air Inlet Z Offset=2 1/16"; B=3 15/16"; Burner Depth=15 1/2"; Burner Height=13 3/4"; Burner Width=14 11/16"; Clearance Front=94"; Clearance Rear=51 1/4"; Clearance Sides=51 1/4"; Cold Water Extension=34 1/4"; Cold Water NPT=3"; Cold Water Radius=1 1/2"; Control Panel Extension=40 1/4"; Current=2 A; Drain Extension=37 1/8"; Drain NPT=1 1/2"; Drain Radius=3/4"; Energy Extension=39"; FC OAL=54 1/2"; Flat Side Distance=66 1/2"; Flue Collector Extension=15 1/2"; Flue Diameter=8"; Flue Location=46 3/4"; Flue Radius=4"; Front Skid Extension=100 1/4"; GT Conn Z=90 15/16"; GT Z=56 1/2"; Gas Conn X=40 1/2"; Gas Conn Y=15 1/2"; Gas Inlet NPT=2"; Gas Inlet Radius=1"; Gas Inlet X=20 1/2"; Gas Inlet Y=5 1/2"; Gas Inlet Z=36 7/16"; Height to Cold Inlet=21 1/4"; Height to Drain=2 1/4"; Height to Energy=32 5/8"; Height to Hot Outlet=60 7/8"; Height to Hot Outlet Actual=60 7/8"; Height to Relief=61 1/2"; Height to Relief Actual=61 1/2"; Hot Outlet Angle=90.00°; Hot Water Extension=34 1/4"; Hot Water NPT=3"; Hot Water Radius=1 1/2"; Input Btu/h=1200000; Nominal Storage=750 gal; Rear Access Extension=0"; Rear Skid Extension=33 1/4"; Recovery Rate 40F to 140F (gph)=1200; Relief Extension=36 1/4"; Size=750; Skid Center Dist=18"; Skid Length=67"; Skid Spacing=36"; Unit Height=81 1/2"; Unit Height Actual=81 1/2"; Unit Radius=33 1/4"; Weight=2770
- 1250 L 750 A-TP: 500-3000 GIY=5 1/2"; A=8 3/8"; Air Inlet Depth=3 1/8"; Air Inlet Diameter=6"; Air Inlet Extension=18 15/16"; Air Inlet Radius=3"; Air Inlet Width=6 3/8"; Air Inlet X=14 7/8"; Air Inlet Y=5 1/4"; Air Inlet Y Offset=2 1/16"; Air Inlet Z Offset=2 1/16"; B=3 15/16"; Burner Depth=15 1/2"; Burner Height=13 3/4"; Burner Width=14 11/16"; Clearance Front=94"; Clearance Rear=51 1/4"; Clearance Sides=51 1/4"; Cold Water Extension=34 1/4"; Cold Water NPT=3"; Cold Water Radius=1 1/2"; Control Panel Extension=40 1/4"; Current=2 A; Drain Extension=37 1/8"; Drain NPT=1 1/2"; Drain Radius=3/4"; Energy Extension=39"; FC OAL=54 1/2"; Flat Side Distance=66 1/2"; Flue Collector Extension=15 1/2"; Flue Diameter=8"; Flue Location=46 3/4"; Flue Radius=4"; Front Skid Extension=100 1/4"; GT Conn Z=90 15/16"; GT Z=56 1/2"; Gas Conn X=40 1/2"; Gas Conn Y=15 1/2"; Gas Inlet NPT=2"; Gas Inlet Radius=1"; Gas Inlet X=20 1/2"; Gas Inlet Y=5 1/2"; Gas Inlet Z=36 7/16"; Height to Cold Inlet=21 1/4"; Height to Drain=2 1/4"; Height to Energy=32 5/8"; Height to Hot Outlet=60 7/8"; Height to Hot Outlet Actual=60 7/8"; Height to Relief=61 1/2"; Height to Relief Actual=61 1/2"; Hot Outlet Angle=90.00°; Hot Water Extension=34 1/4"; Hot Water NPT=3"; Hot Water Radius=1 1/2"; Input Btu/h=1000000; Nominal Storage=750 gal; Rear Access Extension=0"; Rear Skid Extension=33 1/4"; Recovery Rate 40F to 140F (gph)=1000; Relief Extension=36 1/4"; Size=750; Skid Center Dist=18"; Skid Length=67"; Skid Spacing=36"; Unit Height=81 1/2"; Unit Height Actual=81 1/2"; Unit Radius=33 1/4"; Weight=2590
- 1000 L 750 A-TP: 500-3000 GIY=4 1/2"; A=8 3/8"; Air Inlet Depth=3 1/8"; Air Inlet Diameter=6"; Air Inlet Extension=18 15/16"; Air Inlet Radius=3"; Air Inlet Width=6 3/8"; Air Inlet X=14 7/8"; Air Inlet Y=5 1/4"; Air Inlet Y Offset=2 1/16"; Air Inlet Z Offset=2 1/16"; B=3 15/16"; Burner Depth=15 1/2"; Burner Height=13 3/4"; Burner Width=14 11/16"; Clearance Front=86"; Clearance Rear=51 1/4"; Clearance Sides=51 1/4"; Cold Water Extension=34 1/4"; Cold Water NPT=3"; Cold Water Radius=1 1/2"; Control Panel Extension=40 1/4"; Current=2 A; Drain Extension=37 1/8"; Drain NPT=1 1/2"; Drain Radius=3/4"; Energy Extension=38 1/4"; FC OAL=46 1/2"; Flat Side Distance=66 1/2"; Flue Collector Extension=8 1/4"; Flue Diameter=8"; Flue Location=42 3/8"; Flue Radius=4"; Front Skid Extension=100 1/4"; GT Conn Z=74 3/16"; GT Z=48 1/2"; Gas Conn X=40 1/2"; Gas Conn Y=14 1/2"; Gas Inlet NPT=1 1/4"; Gas Inlet Radius=5/8"; Gas Inlet X=20 1/2"; Gas Inlet Y=4 1/2"; Gas Inlet Z=27 11/16"; Height to Cold Inlet=21 1/4"; Height to Drain=2 1/4"; Height to Energy=32 5/8"; Height to Hot Outlet=60 7/8"; Height to Hot Outlet Actual=60 7/8"; Height to Relief=61 1/2"; Height to Relief Actual=61 1/2"; Hot Outlet Angle=90.00°; Hot Water Extension=34 1/4"; Hot Water NPT=3"; Hot Water Radius=1 1/2"; Input Btu/h=800000; Nominal Storage=750 gal; Rear Access Extension=0"; Rear Skid Extension=33 1/4"; Recovery Rate 40F to 140F (gph)=800; Relief Extension=36 1/4"; Size=750; Skid Center Dist=18"; Skid Length=67"; Skid Spacing=36"; Unit Height=81 1/2"; Unit Height Actual=81 1/2"; Unit Radius=33 1/4"; Weight=2320
- 750 L 750 A-TP: 500-3000 GIY=3 5/8"; A=8 3/8"; Air Inlet Depth=3 1/8"; Air Inlet Diameter=6"; Air Inlet Extension=18 15/16"; Air Inlet Radius=3"; Air Inlet Width=6 3/8"; Air Inlet X=14 7/8"; Air Inlet Y=5 1/4"; Air Inlet Y Offset=2 1/16"; Air Inlet Z Offset=2 1/16"; B=3 15/16"; Burner Depth=15 1/2"; Burner Height=13 3/4"; Burner Width=14 11/16"; Clearance Front=86"; Clearance Rear=51 1/4"; Clearance Sides=51 1/4"; Cold Water Extension=34 1/4"; Cold Water NPT=3"; Cold Water Radius=1 1/2"; Control Panel Extension=40 1/4"; Current=2 A; Drain Extension=37 1/8"; Drain NPT=1 1/2"; Drain Radius=3/4"; Energy Extension=38 1/4"; FC OAL=46 1/2"; Flat Side Distance=66 1/2"; Flue Collector Extension=8 1/4"; Flue Diameter=6"; Flue Location=42 3/8"; Flue Radius=3"; Front Skid Extension=100 1/4"; GT Conn Z=69 1/8"; GT Z=48 1/2"; Gas Conn X=36 7/8"; Gas Conn Y=13 5/8"; Gas Inlet NPT=1"; Gas Inlet Radius=1/2"; Gas Inlet X=16 7/8"; Gas Inlet Y=3 5/8"; Gas Inlet Z=22 5/8"; Height to Cold Inlet=21 1/4"; Height to Drain=2 1/4"; Height to Energy=32 5/8"; Height to Hot Outlet=60 7/8"; Height to Hot Outlet Actual=60 7/8"; Height to Relief=61 1/2"; Height to Relief Actual=61 1/2"; Hot Outlet Angle=90.00°; Hot Water Extension=34 1/4"; Hot Water NPT=3"; Hot Water Radius=1 1/2"; Input Btu/h=600000; Nominal Storage=750 gal; Rear Access Extension=0"; Rear Skid Extension=33 1/4"; Recovery Rate 40F to 140F (gph)=600; Relief Extension=36 1/4"; Size=750; Skid Center Dist=18"; Skid Length=67"; Skid Spacing=36"; Unit Height=81 1/2"; Unit Height Actual=81 1/2"; Unit Radius=33 1/4"; Weight=2280
- 2500 L 600 A-TP: 500-3000 GIY=5 7/8"; A=13 3/4"; Air Inlet Depth=7"; Air Inlet Diameter=8"; Air Inlet Extension=20 15/16"; Air Inlet Radius=4"; Air Inlet Width=9"; Air Inlet X=15 15/16"; Air Inlet Y=7 3/16"; Air Inlet Y Offset=2 11/16"; Air Inlet Z Offset=5 3/8"; B=4"; Burner Depth=25 15/16"; Burner Height=16 5/8"; Burner Width=22 1/4"; Clearance Front=103 3/8"; Clearance Rear=45 7/8"; Clearance Sides=45 7/8"; Cold Water Extension=28 7/8"; Cold Water NPT=3"; Cold Water Radius=1 1/2"; Control Panel Extension=34 7/8"; Current=22 A; Drain Extension=31 3/4"; Drain NPT=1 1/2"; Drain Radius=3/4"; Energy Extension=37 15/16"; FC OAL=53 7/16"; Flat Side Distance=55 3/4"; Flue Collector Extension=15 1/2"; Flue Diameter=10"; Flue Location=45 11/16"; Flue Radius=5"; Front Skid Extension=82 7/8"; GT Conn Z=93 13/16"; GT Z=55 7/16"; Gas Conn X=44 1/8"; Gas Conn Y=15 7/8"; Gas Inlet NPT=2 1/2"; Gas Inlet Radius=1 1/4"; Gas Inlet X=24 1/8"; Gas Inlet Y=5 7/8"; Gas Inlet Z=40 3/8"; Height to Cold Inlet=18 1/4"; Height to Drain=2 1/4"; Height to Energy=30"; Height to Hot Outlet=69 3/8"; Height to Hot Outlet Actual=69 3/8"; Height to Relief=70"; Height to Relief Actual=70"; Hot Outlet Angle=90.00°; Hot Water Extension=28 7/8"; Hot Water NPT=3"; Hot Water Radius=1 1/2"; Input Btu/h=2010000; Nominal Storage=600 gal; Rear Access Extension=-43 7/8"; Rear Skid Extension=27 7/8"; Recovery Rate 40F to 140F (gph)=2000; Relief Extension=30 7/8"; Size=600; Skid Center Dist=13 1/2"; Skid Length=55"; Skid Spacing=27"; Unit Height=88 1/2"; Unit Height Actual=88 1/2"; Unit Radius=27 7/8"; Weight=2900
- 2000 L 600 A-TP: 500-3000 GIY=5 1/2"; A=13 3/4"; Air Inlet Depth=7"; Air Inlet Diameter=8"; Air Inlet Extension=20 15/16"; Air Inlet Radius=4"; Air Inlet Width=9"; Air Inlet X=15 15/16"; Air Inlet Y=7 3/16"; Air Inlet Y Offset=2 11/16"; Air Inlet Z Offset=5 3/8"; B=4"; Burner Depth=25 15/16"; Burner Height=16 5/8"; Burner Width=22 1/4"; Clearance Front=103 3/8"; Clearance Rear=45 7/8"; Clearance Sides=45 7/8"; Cold Water Extension=28 7/8"; Cold Water NPT=3"; Cold Water Radius=1 1/2"; Control Panel Extension=34 7/8"; Current=12 A; Drain Extension=31 3/4"; Drain NPT=1 1/2"; Drain Radius=3/4"; Energy Extension=37 15/16"; FC OAL=53 7/16"; Flat Side Distance=55 3/4"; Flue Collector Extension=15 1/2"; Flue Diameter=10"; Flue Location=45 11/16"; Flue Radius=5"; Front Skid Extension=82 7/8"; GT Conn Z=89 1/2"; GT Z=55 7/16"; Gas Conn X=42"; Gas Conn Y=15 1/2"; Gas Inlet NPT=2"; Gas Inlet Radius=1"; Gas Inlet X=22"; Gas Inlet Y=5 1/2"; Gas Inlet Z=36 1/16"; Height to Cold Inlet=18 1/4"; Height to Drain=2 1/4"; Height to Energy=30"; Height to Hot Outlet=69 3/8"; Height to Hot Outlet Actual=69 3/8"; Height to Relief=70"; Height to Relief Actual=70"; Hot Outlet Angle=90.00°; Hot Water Extension=28 7/8"; Hot Water NPT=3"; Hot Water Radius=1 1/2"; Input Btu/h=1600000; Nominal Storage=600 gal; Rear Access Extension=-43 7/8"; Rear Skid Extension=27 7/8"; Recovery Rate 40F to 140F (gph)=1600; Relief Extension=30 7/8"; Size=600; Skid Center Dist=13 1/2"; Skid Length=55"; Skid Spacing=27"; Unit Height=88 1/2"; Unit Height Actual=88 1/2"; Unit Radius=27 7/8"; Weight=2880
- 1500 L 600 A-TP: 500-3000 GIY=5 1/2"; A=8 3/8"; Air Inlet Depth=3 1/8"; Air Inlet Diameter=6"; Air Inlet Extension=18 15/16"; Air Inlet Radius=3"; Air Inlet Width=6 3/8"; Air Inlet X=14 7/8"; Air Inlet Y=5 1/4"; Air Inlet Y Offset=2 1/16"; Air Inlet Z Offset=2 1/16"; B=3 15/16"; Burner Depth=15 1/2"; Burner Height=13 3/4"; Burner Width=14 11/16"; Clearance Front=88 3/8"; Clearance Rear=45 7/8"; Clearance Sides=45 7/8"; Cold Water Extension=28 7/8"; Cold Water NPT=3"; Cold Water Radius=1 1/2"; Control Panel Extension=34 7/8"; Current=12 A; Drain Extension=31 3/4"; Drain NPT=1 1/2"; Drain Radius=3/4"; Energy Extension=33 3/8"; FC OAL=48 7/8"; Flat Side Distance=55 3/4"; Flue Collector Extension=15 1/2"; Flue Diameter=8"; Flue Location=41 1/8"; Flue Radius=4"; Front Skid Extension=82 7/8"; GT Conn Z=85 5/16"; GT Z=50 7/8"; Gas Conn X=40 1/2"; Gas Conn Y=15 1/2"; Gas Inlet NPT=2"; Gas Inlet Radius=1"; Gas Inlet X=20 1/2"; Gas Inlet Y=5 1/2"; Gas Inlet Z=36 7/16"; Height to Cold Inlet=18 1/4"; Height to Drain=2 1/4"; Height to Energy=30"; Height to Hot Outlet=69 3/8"; Height to Hot Outlet Actual=69 3/8"; Height to Relief=70"; Height to Relief Actual=70"; Hot Outlet Angle=90.00°; Hot Water Extension=28 7/8"; Hot Water NPT=3"; Hot Water Radius=1 1/2"; Input Btu/h=1200000; Nominal Storage=600 gal; Rear Access Extension=0"; Rear Skid Extension=27 7/8"; Recovery Rate 40F to 140F (gph)=1200; Relief Extension=30 7/8"; Size=600; Skid Center Dist=13 1/2"; Skid Length=55"; Skid Spacing=27"; Unit Height=88 1/2"; Unit Height Actual=88 1/2"; Unit Radius=27 7/8"; Weight=2445
- 1250 L 600 A-TP: 500-3000 GIY=5 1/2"; A=8 3/8"; Air Inlet Depth=3 1/8"; Air Inlet Diameter=6"; Air Inlet Extension=18 15/16"; Air Inlet Radius=3"; Air Inlet Width=6 3/8"; Air Inlet X=14 7/8"; Air Inlet Y=5 1/4"; Air Inlet Y Offset=2 1/16"; Air Inlet Z Offset=2 1/16"; B=3 15/16"; Burner Depth=15 1/2"; Burner Height=13 3/4"; Burner Width=14 11/16"; Clearance Front=88 3/8"; Clearance Rear=45 7/8"; Clearance Sides=45 7/8"; Cold Water Extension=28 7/8"; Cold Water NPT=3"; Cold Water Radius=1 1/2"; Control Panel Extension=34 7/8"; Current=10 A; Drain Extension=31 3/4"; Drain NPT=1 1/2"; Drain Radius=3/4"; Energy Extension=33 3/8"; FC OAL=48 7/8"; Flat Side Distance=55 3/4"; Flue Collector Extension=15 1/2"; Flue Diameter=8"; Flue Location=41 1/8"; Flue Radius=4"; Front Skid Extension=82 7/8"; GT Conn Z=85 5/16"; GT Z=50 7/8"; Gas Conn X=40 1/2"; Gas Conn Y=15 1/2"; Gas Inlet NPT=2"; Gas Inlet Radius=1"; Gas Inlet X=20 1/2"; Gas Inlet Y=5 1/2"; Gas Inlet Z=36 7/16"; Height to Cold Inlet=18 1/4"; Height to Drain=2 1/4"; Height to Energy=30"; Height to Hot Outlet=69 3/8"; Height to Hot Outlet Actual=69 3/8"; Height to Relief=70"; Height to Relief Actual=70"; Hot Outlet Angle=90.00°; Hot Water Extension=28 7/8"; Hot Water NPT=3"; Hot Water Radius=1 1/2"; Input Btu/h=1000000; Nominal Storage=600 gal; Rear Access Extension=0"; Rear Skid Extension=27 7/8"; Recovery Rate 40F to 140F (gph)=1000; Relief Extension=30 7/8"; Size=600; Skid Center Dist=13 1/2"; Skid Length=55"; Skid Spacing=27"; Unit Height=88 1/2"; Unit Height Actual=88 1/2"; Unit Radius=27 7/8"; Weight=2435
- 1000 L 600 A-TP: 500-3000 GIY=4 1/2"; A=8 3/8"; Air Inlet Depth=3 1/8"; Air Inlet Diameter=6"; Air Inlet Extension=18 15/16"; Air Inlet Radius=3"; Air Inlet Width=6 3/8"; Air Inlet X=14 7/8"; Air Inlet Y=5 1/4"; Air Inlet Y Offset=2 1/16"; Air Inlet Z Offset=2 1/16"; B=3 15/16"; Burner Depth=15 1/2"; Burner Height=13 3/4"; Burner Width=14 11/16"; Clearance Front=80 3/8"; Clearance Rear=45 7/8"; Clearance Sides=45 7/8"; Cold Water Extension=28 7/8"; Cold Water NPT=3"; Cold Water Radius=1 1/2"; Control Panel Extension=34 7/8"; Current=10 A; Drain Extension=31 3/4"; Drain NPT=1 1/2"; Drain Radius=3/4"; Energy Extension=32 5/8"; FC OAL=40 7/8"; Flat Side Distance=55 3/4"; Flue Collector Extension=8 1/4"; Flue Diameter=8"; Flue Location=36 3/4"; Flue Radius=4"; Front Skid Extension=82 7/8"; GT Conn Z=68 9/16"; GT Z=42 7/8"; Gas Conn X=40 1/2"; Gas Conn Y=14 1/2"; Gas Inlet NPT=1 1/4"; Gas Inlet Radius=5/8"; Gas Inlet X=20 1/2"; Gas Inlet Y=4 1/2"; Gas Inlet Z=27 11/16"; Height to Cold Inlet=18 1/4"; Height to Drain=2 1/4"; Height to Energy=30"; Height to Hot Outlet=69 3/8"; Height to Hot Outlet Actual=69 3/8"; Height to Relief=70"; Height to Relief Actual=70"; Hot Outlet Angle=90.00°; Hot Water Extension=28 7/8"; Hot Water NPT=3"; Hot Water Radius=1 1/2"; Input Btu/h=800000; Nominal Storage=600 gal; Rear Access Extension=0"; Rear Skid Extension=27 7/8"; Recovery Rate 40F to 140F (gph)=800; Relief Extension=30 7/8"; Size=600; Skid Center Dist=13 1/2"; Skid Length=55"; Skid Spacing=27"; Unit Height=88 1/2"; Unit Height Actual=88 1/2"; Unit Radius=27 7/8"; Weight=2180
- 750 L 600 A-TP: 500-3000 GIY=3 5/8"; A=8 3/8"; Air Inlet Depth=3 1/8"; Air Inlet Diameter=6"; Air Inlet Extension=18 15/16"; Air Inlet Radius=3"; Air Inlet Width=6 3/8"; Air Inlet X=14 7/8"; Air Inlet Y=5 1/4"; Air Inlet Y Offset=2 1/16"; Air Inlet Z Offset=2 1/16"; B=3 15/16"; Burner Depth=15 1/2"; Burner Height=13 3/4"; Burner Width=14 11/16"; Clearance Front=80 3/8"; Clearance Rear=45 7/8"; Clearance Sides=45 7/8"; Cold Water Extension=28 7/8"; Cold Water NPT=3"; Cold Water Radius=1 1/2"; Control Panel Extension=34 7/8"; Current=5 A; Drain Extension=31 3/4"; Drain NPT=1 1/2"; Drain Radius=3/4"; Energy Extension=32 5/8"; FC OAL=40 7/8"; Flat Side Distance=55 3/4"; Flue Collector Extension=8 1/4"; Flue Diameter=6"; Flue Location=36 3/4"; Flue Radius=3"; Front Skid Extension=82 7/8"; GT Conn Z=63 1/2"; GT Z=42 7/8"; Gas Conn X=36 7/8"; Gas Conn Y=13 5/8"; Gas Inlet NPT=1"; Gas Inlet Radius=1/2"; Gas Inlet X=16 7/8"; Gas Inlet Y=3 5/8"; Gas Inlet Z=22 5/8"; Height to Cold Inlet=18 1/4"; Height to Drain=2 1/4"; Height to Energy=30"; Height to Hot Outlet=69 3/8"; Height to Hot Outlet Actual=69 3/8"; Height to Relief=70"; Height to Relief Actual=70"; Hot Outlet Angle=90.00°; Hot Water Extension=28 7/8"; Hot Water NPT=3"; Hot Water Radius=1 1/2"; Input Btu/h=600000; Nominal Storage=600 gal; Rear Access Extension=0"; Rear Skid Extension=27 7/8"; Recovery Rate 40F to 140F (gph)=600; Relief Extension=30 7/8"; Size=600; Skid Center Dist=13 1/2"; Skid Length=55"; Skid Spacing=27"; Unit Height=88 1/2"; Unit Height Actual=88 1/2"; Unit Radius=27 7/8"; Weight=2140
- 2500 L 500A-TP: 500-3000 GIY=5 7/8"; A=13 3/4"; Air Inlet Depth=7"; Air Inlet Diameter=8"; Air Inlet Extension=20 15/16"; Air Inlet Radius=4"; Air Inlet Width=9"; Air Inlet X=15 15/16"; Air Inlet Y=7 3/16"; Air Inlet Y Offset=2 11/16"; Air Inlet Z Offset=5 3/8"; B=4"; Burner Depth=25 15/16"; Burner Height=16 5/8"; Burner Width=22 1/4"; Clearance Front=103 3/8"; Clearance Rear=45 7/8"; Clearance Sides=45 7/8"; Cold Water Extension=28 7/8"; Cold Water NPT=3"; Cold Water Radius=1 1/2"; Control Panel Extension=34 7/8"; Current=22 A; Drain Extension=31 3/4"; Drain NPT=1 1/2"; Drain Radius=3/4"; Energy Extension=37 15/16"; FC OAL=53 7/16"; Flat Side Distance=55 3/4"; Flue Collector Extension=15 1/2"; Flue Diameter=10"; Flue Location=45 11/16"; Flue Radius=5"; Front Skid Extension=82 7/8"; GT Conn Z=93 13/16"; GT Z=55 7/16"; Gas Conn X=44 1/8"; Gas Conn Y=15 7/8"; Gas Inlet NPT=2 1/2"; Gas Inlet Radius=1 1/4"; Gas Inlet X=24 1/8"; Gas Inlet Y=5 7/8"; Gas Inlet Z=40 3/8"; Height to Cold Inlet=18 1/4"; Height to Drain=2 1/4"; Height to Energy=30"; Height to Hot Outlet=57 3/8"; Height to Hot Outlet Actual=57 3/8"; Height to Relief=58"; Height to Relief Actual=58"; Hot Outlet Angle=90.00°; Hot Water Extension=28 7/8"; Hot Water NPT=3"; Hot Water Radius=1 1/2"; Input Btu/h=2010000; Nominal Storage=500 gal; Rear Access Extension=-43 7/8"; Rear Skid Extension=27 7/8"; Recovery Rate 40F to 140F (gph)=2000; Relief Extension=30 7/8"; Size=500; Skid Center Dist=13 1/2"; Skid Length=55"; Skid Spacing=27"; Unit Height=76 1/2"; Unit Height Actual=76 1/2"; Unit Radius=27 7/8"; Weight=2675
- 2000 L 500A-TP: 500-3000 GIY=5 1/2"; A=13 3/4"; Air Inlet Depth=7"; Air Inlet Diameter=8"; Air Inlet Extension=20 15/16"; Air Inlet Radius=4"; Air Inlet Width=9"; Air Inlet X=15 15/16"; Air Inlet Y=7 3/16"; Air Inlet Y Offset=2 11/16"; Air Inlet Z Offset=5 3/8"; B=4"; Burner Depth=25 15/16"; Burner Height=16 5/8"; Burner Width=22 1/4"; Clearance Front=103 3/8"; Clearance Rear=45 7/8"; Clearance Sides=45 7/8"; Cold Water Extension=28 7/8"; Cold Water NPT=3"; Cold Water Radius=1 1/2"; Control Panel Extension=34 7/8"; Current=12 A; Drain Extension=31 3/4"; Drain NPT=1 1/2"; Drain Radius=3/4"; Energy Extension=37 15/16"; FC OAL=53 7/16"; Flat Side Distance=55 3/4"; Flue Collector Extension=15 1/2"; Flue Diameter=10"; Flue Location=45 11/16"; Flue Radius=5"; Front Skid Extension=82 7/8"; GT Conn Z=89 1/2"; GT Z=55 7/16"; Gas Conn X=42"; Gas Conn Y=15 1/2"; Gas Inlet NPT=2"; Gas Inlet Radius=1"; Gas Inlet X=22"; Gas Inlet Y=5 1/2"; Gas Inlet Z=36 1/16"; Height to Cold Inlet=18 1/4"; Height to Drain=2 1/4"; Height to Energy=30"; Height to Hot Outlet=57 3/8"; Height to Hot Outlet Actual=57 3/8"; Height to Relief=58"; Height to Relief Actual=58"; Hot Outlet Angle=90.00°; Hot Water Extension=28 7/8"; Hot Water NPT=3"; Hot Water Radius=1 1/2"; Input Btu/h=1600000; Nominal Storage=500 gal; Rear Access Extension=-43 7/8"; Rear Skid Extension=27 7/8"; Recovery Rate 40F to 140F (gph)=1600; Relief Extension=30 7/8"; Size=500; Skid Center Dist=13 1/2"; Skid Length=55"; Skid Spacing=27"; Unit Height=76 1/2"; Unit Height Actual=76 1/2"; Unit Radius=27 7/8"; Weight=2655
- 1500 L 500A-TP: 500-3000 GIY=5 1/2"; A=8 3/8"; Air Inlet Depth=3 1/8"; Air Inlet Diameter=6"; Air Inlet Extension=18 15/16"; Air Inlet Radius=3"; Air Inlet Width=6 3/8"; Air Inlet X=14 7/8"; Air Inlet Y=5 1/4"; Air Inlet Y Offset=2 1/16"; Air Inlet Z Offset=2 1/16"; B=3 15/16"; Burner Depth=15 1/2"; Burner Height=13 3/4"; Burner Width=14 11/16"; Clearance Front=88 3/8"; Clearance Rear=45 7/8"; Clearance Sides=45 7/8"; Cold Water Extension=28 7/8"; Cold Water NPT=3"; Cold Water Radius=1 1/2"; Control Panel Extension=34 7/8"; Current=12 A; Drain Extension=31 3/4"; Drain NPT=1 1/2"; Drain Radius=3/4"; Energy Extension=33 3/8"; FC OAL=48 7/8"; Flat Side Distance=55 3/4"; Flue Collector Extension=15 1/2"; Flue Diameter=8"; Flue Location=41 1/8"; Flue Radius=4"; Front Skid Extension=82 7/8"; GT Conn Z=85 5/16"; GT Z=50 7/8"; Gas Conn X=40 1/2"; Gas Conn Y=15 1/2"; Gas Inlet NPT=2"; Gas Inlet Radius=1"; Gas Inlet X=20 1/2"; Gas Inlet Y=5 1/2"; Gas Inlet Z=36 7/16"; Height to Cold Inlet=18 1/4"; Height to Drain=2 1/4"; Height to Energy=30"; Height to Hot Outlet=57 3/8"; Height to Hot Outlet Actual=57 3/8"; Height to Relief=58"; Height to Relief Actual=58"; Hot Outlet Angle=90.00°; Hot Water Extension=28 7/8"; Hot Water NPT=3"; Hot Water Radius=1 1/2"; Input Btu/h=1200000; Nominal Storage=500 gal; Rear Access Extension=0"; Rear Skid Extension=27 7/8"; Recovery Rate 40F to 140F (gph)=1200; Relief Extension=30 7/8"; Size=500; Skid Center Dist=13 1/2"; Skid Length=55"; Skid Spacing=27"; Unit Height=76 1/2"; Unit Height Actual=76 1/2"; Unit Radius=27 7/8"; Weight=2220
- 1250 L 500A-TP: 500-3000 GIY=5 1/2"; A=8 3/8"; Air Inlet Depth=3 1/8"; Air Inlet Diameter=6"; Air Inlet Extension=18 15/16"; Air Inlet Radius=3"; Air Inlet Width=6 3/8"; Air Inlet X=14 7/8"; Air Inlet Y=5 1/4"; Air Inlet Y Offset=2 1/16"; Air Inlet Z Offset=2 1/16"; B=3 15/16"; Burner Depth=15 1/2"; Burner Height=13 3/4"; Burner Width=14 11/16"; Clearance Front=88 3/8"; Clearance Rear=45 7/8"; Clearance Sides=45 7/8"; Cold Water Extension=28 7/8"; Cold Water NPT=3"; Cold Water Radius=1 1/2"; Control Panel Extension=34 7/8"; Current=10 A; Drain Extension=31 3/4"; Drain NPT=1 1/2"; Drain Radius=3/4"; Energy Extension=33 3/8"; FC OAL=48 7/8"; Flat Side Distance=55 3/4"; Flue Collector Extension=15 1/2"; Flue Diameter=8"; Flue Location=41 1/8"; Flue Radius=4"; Front Skid Extension=82 7/8"; GT Conn Z=85 5/16"; GT Z=50 7/8"; Gas Conn X=40 1/2"; Gas Conn Y=15 1/2"; Gas Inlet NPT=2"; Gas Inlet Radius=1"; Gas Inlet X=20 1/2"; Gas Inlet Y=5 1/2"; Gas Inlet Z=36 7/16"; Height to Cold Inlet=18 1/4"; Height to Drain=2 1/4"; Height to Energy=30"; Height to Hot Outlet=57 3/8"; Height to Hot Outlet Actual=57 3/8"; Height to Relief=58"; Height to Relief Actual=58"; Hot Outlet Angle=90.00°; Hot Water Extension=28 7/8"; Hot Water NPT=3"; Hot Water Radius=1 1/2"; Input Btu/h=1000000; Nominal Storage=500 gal; Rear Access Extension=0"; Rear Skid Extension=27 7/8"; Recovery Rate 40F to 140F (gph)=1000; Relief Extension=30 7/8"; Size=500; Skid Center Dist=13 1/2"; Skid Length=55"; Skid Spacing=27"; Unit Height=76 1/2"; Unit Height Actual=76 1/2"; Unit Radius=27 7/8"; Weight=2210
- 1000 L 500A-TP: 500-3000 GIY=4 1/2"; A=8 3/8"; Air Inlet Depth=3 1/8"; Air Inlet Diameter=6"; Air Inlet Extension=18 15/16"; Air Inlet Radius=3"; Air Inlet Width=6 3/8"; Air Inlet X=14 7/8"; Air Inlet Y=5 1/4"; Air Inlet Y Offset=2 1/16"; Air Inlet Z Offset=2 1/16"; B=3 15/16"; Burner Depth=15 1/2"; Burner Height=13 3/4"; Burner Width=14 11/16"; Clearance Front=80 3/8"; Clearance Rear=45 7/8"; Clearance Sides=45 7/8"; Cold Water Extension=28 7/8"; Cold Water NPT=3"; Cold Water Radius=1 1/2"; Control Panel Extension=34 7/8"; Current=10 A; Drain Extension=31 3/4"; Drain NPT=1 1/2"; Drain Radius=3/4"; Energy Extension=32 5/8"; FC OAL=40 7/8"; Flat Side Distance=55 3/4"; Flue Collector Extension=8 1/4"; Flue Diameter=8"; Flue Location=36 3/4"; Flue Radius=4"; Front Skid Extension=82 7/8"; GT Conn Z=68 9/16"; GT Z=42 7/8"; Gas Conn X=40 1/2"; Gas Conn Y=14 1/2"; Gas Inlet NPT=1 1/4"; Gas Inlet Radius=5/8"; Gas Inlet X=20 1/2"; Gas Inlet Y=4 1/2"; Gas Inlet Z=27 11/16"; Height to Cold Inlet=18 1/4"; Height to Drain=2 1/4"; Height to Energy=30"; Height to Hot Outlet=57 3/8"; Height to Hot Outlet Actual=57 3/8"; Height to Relief=58"; Height to Relief Actual=58"; Hot Outlet Angle=90.00°; Hot Water Extension=28 7/8"; Hot Water NPT=3"; Hot Water Radius=1 1/2"; Input Btu/h=800000; Nominal Storage=500 gal; Rear Access Extension=0"; Rear Skid Extension=27 7/8"; Recovery Rate 40F to 140F (gph)=800; Relief Extension=30 7/8"; Size=500; Skid Center Dist=13 1/2"; Skid Length=55"; Skid Spacing=27"; Unit Height=76 1/2"; Unit Height Actual=76 1/2"; Unit Radius=27 7/8"; Weight=1955
- 750 L 500A-TP: 500-3000 GIY=3 5/8"; A=8 3/8"; Air Inlet Depth=3 1/8"; Air Inlet Diameter=6"; Air Inlet Extension=18 15/16"; Air Inlet Radius=3"; Air Inlet Width=6 3/8"; Air Inlet X=14 7/8"; Air Inlet Y=5 1/4"; Air Inlet Y Offset=2 1/16"; Air Inlet Z Offset=2 1/16"; B=3 15/16"; Burner Depth=15 1/2"; Burner Height=13 3/4"; Burner Width=14 11/16"; Clearance Front=80 3/8"; Clearance Rear=45 7/8"; Clearance Sides=45 7/8"; Cold Water Extension=28 7/8"; Cold Water NPT=3"; Cold Water Radius=1 1/2"; Control Panel Extension=34 7/8"; Current=5 A; Drain Extension=31 3/4"; Drain NPT=1 1/2"; Drain Radius=3/4"; Energy Extension=32 5/8"; FC OAL=40 7/8"; Flat Side Distance=55 3/4"; Flue Collector Extension=8 1/4"; Flue Diameter=6"; Flue Location=36 3/4"; Flue Radius=3"; Front Skid Extension=82 7/8"; GT Conn Z=63 1/2"; GT Z=42 7/8"; Gas Conn X=36 7/8"; Gas Conn Y=13 5/8"; Gas Inlet NPT=1"; Gas Inlet Radius=1/2"; Gas Inlet X=16 7/8"; Gas Inlet Y=3 5/8"; Gas Inlet Z=22 5/8"; Height to Cold Inlet=18 1/4"; Height to Drain=2 1/4"; Height to Energy=30"; Height to Hot Outlet=57 3/8"; Height to Hot Outlet Actual=57 3/8"; Height to Relief=58"; Height to Relief Actual=58"; Hot Outlet Angle=90.00°; Hot Water Extension=28 7/8"; Hot Water NPT=3"; Hot Water Radius=1 1/2"; Input Btu/h=600000; Nominal Storage=500 gal; Rear Access Extension=0"; Rear Skid Extension=27 7/8"; Recovery Rate 40F to 140F (gph)=600; Relief Extension=30 7/8"; Size=500; Skid Center Dist=13 1/2"; Skid Length=55"; Skid Spacing=27"; Unit Height=76 1/2"; Unit Height Actual=76 1/2"; Unit Radius=27 7/8"; Weight=1915
- 2500 L 400A-TP: 500-3000 GIY=5 7/8"; A=13 3/4"; Air Inlet Depth=7"; Air Inlet Diameter=8"; Air Inlet Extension=20 15/16"; Air Inlet Radius=4"; Air Inlet Width=9"; Air Inlet X=15 15/16"; Air Inlet Y=7 3/16"; Air Inlet Y Offset=2 11/16"; Air Inlet Z Offset=5 3/8"; B=4"; Burner Depth=25 15/16"; Burner Height=16 5/8"; Burner Width=22 1/4"; Clearance Front=103 9/16"; Clearance Rear=40 5/8"; Clearance Sides=40 5/8"; Cold Water Extension=23 5/8"; Cold Water NPT=2"; Cold Water Radius=1"; Control Panel Extension=29 5/8"; Current=22 A; Drain Extension=26 1/2"; Drain NPT=1"; Drain Radius=1/2"; Energy Extension=38 1/8"; FC OAL=53 5/8"; Flat Side Distance=45 1/4"; Flue Collector Extension=15 1/2"; Flue Diameter=10"; Flue Location=45 7/8"; Flue Radius=5"; Front Skid Extension=77 5/8"; GT Conn Z=94"; GT Z=55 5/8"; Gas Conn X=44 1/8"; Gas Conn Y=15 7/8"; Gas Inlet NPT=2 1/2"; Gas Inlet Radius=1 1/4"; Gas Inlet X=24 1/8"; Gas Inlet Y=5 7/8"; Gas Inlet Z=40 3/8"; Height to Cold Inlet=17 1/16"; Height to Drain=1 7/8"; Height to Energy=28 3/4"; Height to Hot Outlet=68 1/2"; Height to Hot Outlet Actual=68 1/2"; Height to Relief=69 1/8"; Height to Relief Actual=69 1/8"; Hot Outlet Angle=90.00°; Hot Water Extension=23 5/8"; Hot Water NPT=2"; Hot Water Radius=1"; Input Btu/h=2010000; Nominal Storage=400 gal; Rear Access Extension=-40 5/8"; Rear Skid Extension=22 5/8"; Recovery Rate 40F to 140F (gph)=2000; Relief Extension=25 5/8"; Size=400; Skid Center Dist=13 1/2"; Skid Length=55"; Skid Spacing=27"; Unit Height=85 1/2"; Unit Height Actual=85 1/2"; Unit Radius=22 5/8"; Weight=2250
- 2000 L 400A-TP: 500-3000 GIY=5 1/2"; A=13 3/4"; Air Inlet Depth=7"; Air Inlet Diameter=8"; Air Inlet Extension=20 15/16"; Air Inlet Radius=4"; Air Inlet Width=9"; Air Inlet X=15 15/16"; Air Inlet Y=7 3/16"; Air Inlet Y Offset=2 11/16"; Air Inlet Z Offset=5 3/8"; B=4"; Burner Depth=25 15/16"; Burner Height=16 5/8"; Burner Width=22 1/4"; Clearance Front=103 9/16"; Clearance Rear=40 5/8"; Clearance Sides=40 5/8"; Cold Water Extension=23 5/8"; Cold Water NPT=2"; Cold Water Radius=1"; Control Panel Extension=29 5/8"; Current=22 A; Drain Extension=26 1/2"; Drain NPT=1"; Drain Radius=1/2"; Energy Extension=38 1/8"; FC OAL=53 5/8"; Flat Side Distance=45 1/4"; Flue Collector Extension=15 1/2"; Flue Diameter=10"; Flue Location=45 7/8"; Flue Radius=5"; Front Skid Extension=77 5/8"; GT Conn Z=89 11/16"; GT Z=55 5/8"; Gas Conn X=42"; Gas Conn Y=15 1/2"; Gas Inlet NPT=2"; Gas Inlet Radius=1"; Gas Inlet X=22"; Gas Inlet Y=5 1/2"; Gas Inlet Z=36 1/16"; Height to Cold Inlet=17 1/16"; Height to Drain=1 7/8"; Height to Energy=28 3/4"; Height to Hot Outlet=68 1/2"; Height to Hot Outlet Actual=68 1/2"; Height to Relief=69 1/8"; Height to Relief Actual=69 1/8"; Hot Outlet Angle=90.00°; Hot Water Extension=23 5/8"; Hot Water NPT=2"; Hot Water Radius=1"; Input Btu/h=1600000; Nominal Storage=400 gal; Rear Access Extension=-40 5/8"; Rear Skid Extension=22 5/8"; Recovery Rate 40F to 140F (gph)=1600; Relief Extension=25 5/8"; Size=400; Skid Center Dist=13 1/2"; Skid Length=55"; Skid Spacing=27"; Unit Height=85 1/2"; Unit Height Actual=85 1/2"; Unit Radius=22 5/8"; Weight=2230
- 1500 L 400A-TP: 500-3000 GIY=5 1/2"; A=8 3/8"; Air Inlet Depth=3 1/8"; Air Inlet Diameter=6"; Air Inlet Extension=18 15/16"; Air Inlet Radius=3"; Air Inlet Width=6 3/8"; Air Inlet X=14 7/8"; Air Inlet Y=5 1/4"; Air Inlet Y Offset=2 1/16"; Air Inlet Z Offset=2 1/16"; B=3 15/16"; Burner Depth=15 1/2"; Burner Height=13 3/4"; Burner Width=14 11/16"; Clearance Front=93 1/8"; Clearance Rear=40 5/8"; Clearance Sides=40 5/8"; Cold Water Extension=23 5/8"; Cold Water NPT=2"; Cold Water Radius=1"; Control Panel Extension=29 5/8"; Current=12 A; Drain Extension=26 1/2"; Drain NPT=1"; Drain Radius=1/2"; Energy Extension=38 1/8"; FC OAL=53 5/8"; Flat Side Distance=45 1/4"; Flue Collector Extension=15 1/2"; Flue Diameter=8"; Flue Location=45 7/8"; Flue Radius=4"; Front Skid Extension=77 5/8"; GT Conn Z=90 1/16"; GT Z=55 5/8"; Gas Conn X=40 1/2"; Gas Conn Y=15 1/2"; Gas Inlet NPT=2"; Gas Inlet Radius=1"; Gas Inlet X=20 1/2"; Gas Inlet Y=5 1/2"; Gas Inlet Z=36 7/16"; Height to Cold Inlet=17 1/16"; Height to Drain=1 7/8"; Height to Energy=28 3/4"; Height to Hot Outlet=68 1/2"; Height to Hot Outlet Actual=68 1/2"; Height to Relief=69 1/8"; Height to Relief Actual=69 1/8"; Hot Outlet Angle=90.00°; Hot Water Extension=23 5/8"; Hot Water NPT=2"; Hot Water Radius=1"; Input Btu/h=1200000; Nominal Storage=400 gal; Rear Access Extension=0"; Rear Skid Extension=22 5/8"; Recovery Rate 40F to 140F (gph)=1200; Relief Extension=25 5/8"; Size=400; Skid Center Dist=13 1/2"; Skid Length=55"; Skid Spacing=27"; Unit Height=85 1/2"; Unit Height Actual=85 1/2"; Unit Radius=22 5/8"; Weight=1885
- 1250 L 400A-TP: 500-3000 GIY=5 1/2"; A=8 3/8"; Air Inlet Depth=3 1/8"; Air Inlet Diameter=6"; Air Inlet Extension=18 15/16"; Air Inlet Radius=3"; Air Inlet Width=6 3/8"; Air Inlet X=14 7/8"; Air Inlet Y=5 1/4"; Air Inlet Y Offset=2 1/16"; Air Inlet Z Offset=2 1/16"; B=3 15/16"; Burner Depth=15 1/2"; Burner Height=13 3/4"; Burner Width=14 11/16"; Clearance Front=93 1/8"; Clearance Rear=40 5/8"; Clearance Sides=40 5/8"; Cold Water Extension=23 5/8"; Cold Water NPT=2"; Cold Water Radius=1"; Control Panel Extension=29 5/8"; Current=12 A; Drain Extension=26 1/2"; Drain NPT=1"; Drain Radius=1/2"; Energy Extension=38 1/8"; FC OAL=53 5/8"; Flat Side Distance=45 1/4"; Flue Collector Extension=15 1/2"; Flue Diameter=8"; Flue Location=45 7/8"; Flue Radius=4"; Front Skid Extension=77 5/8"; GT Conn Z=90 1/16"; GT Z=55 5/8"; Gas Conn X=40 1/2"; Gas Conn Y=15 1/2"; Gas Inlet NPT=2"; Gas Inlet Radius=1"; Gas Inlet X=20 1/2"; Gas Inlet Y=5 1/2"; Gas Inlet Z=36 7/16"; Height to Cold Inlet=17 1/16"; Height to Drain=1 7/8"; Height to Energy=28 3/4"; Height to Hot Outlet=68 1/2"; Height to Hot Outlet Actual=68 1/2"; Height to Relief=69 1/8"; Height to Relief Actual=69 1/8"; Hot Outlet Angle=90.00°; Hot Water Extension=23 5/8"; Hot Water NPT=2"; Hot Water Radius=1"; Input Btu/h=1000000; Nominal Storage=400 gal; Rear Access Extension=0"; Rear Skid Extension=22 5/8"; Recovery Rate 40F to 140F (gph)=1000; Relief Extension=25 5/8"; Size=400; Skid Center Dist=13 1/2"; Skid Length=55"; Skid Spacing=27"; Unit Height=85 1/2"; Unit Height Actual=85 1/2"; Unit Radius=22 5/8"; Weight=1805
- 1000 L 400A-TP: 500-3000 GIY=4 1/2"; A=8 3/8"; Air Inlet Depth=3 1/8"; Air Inlet Diameter=6"; Air Inlet Extension=18 15/16"; Air Inlet Radius=3"; Air Inlet Width=6 3/8"; Air Inlet X=14 7/8"; Air Inlet Y=5 1/4"; Air Inlet Y Offset=2 1/16"; Air Inlet Z Offset=2 1/16"; B=3 15/16"; Burner Depth=15 1/2"; Burner Height=13 3/4"; Burner Width=14 11/16"; Clearance Front=74 7/8"; Clearance Rear=40 5/8"; Clearance Sides=40 5/8"; Cold Water Extension=23 5/8"; Cold Water NPT=2"; Cold Water Radius=1"; Control Panel Extension=29 5/8"; Current=10 A; Drain Extension=26 1/2"; Drain NPT=1"; Drain Radius=1/2"; Energy Extension=27 1/8"; FC OAL=35 3/8"; Flat Side Distance=45 1/4"; Flue Collector Extension=8 1/4"; Flue Diameter=8"; Flue Location=31 1/4"; Flue Radius=4"; Front Skid Extension=68 1/8"; GT Conn Z=63 1/16"; GT Z=37 3/8"; Gas Conn X=40 1/2"; Gas Conn Y=14 1/2"; Gas Inlet NPT=1 1/4"; Gas Inlet Radius=5/8"; Gas Inlet X=20 1/2"; Gas Inlet Y=4 1/2"; Gas Inlet Z=27 11/16"; Height to Cold Inlet=17 1/16"; Height to Drain=1 7/8"; Height to Energy=28 3/4"; Height to Hot Outlet=68 1/2"; Height to Hot Outlet Actual=68 1/2"; Height to Relief=69 1/8"; Height to Relief Actual=69 1/8"; Hot Outlet Angle=90.00°; Hot Water Extension=23 5/8"; Hot Water NPT=2"; Hot Water Radius=1"; Input Btu/h=800000; Nominal Storage=400 gal; Rear Access Extension=0"; Rear Skid Extension=22 5/8"; Recovery Rate 40F to 140F (gph)=800; Relief Extension=25 5/8"; Size=400; Skid Center Dist=13 1/2"; Skid Length=45 1/2"; Skid Spacing=27"; Unit Height=85 1/2"; Unit Height Actual=85 1/2"; Unit Radius=22 5/8"; Weight=1575
- 750 L 400A-TP: 500-3000 GIY=3 5/8"; A=8 3/8"; Air Inlet Depth=3 1/8"; Air Inlet Diameter=6"; Air Inlet Extension=18 15/16"; Air Inlet Radius=3"; Air Inlet Width=6 3/8"; Air Inlet X=14 7/8"; Air Inlet Y=5 1/4"; Air Inlet Y Offset=2 1/16"; Air Inlet Z Offset=2 1/16"; B=3 15/16"; Burner Depth=15 1/2"; Burner Height=13 3/4"; Burner Width=14 11/16"; Clearance Front=74 7/8"; Clearance Rear=40 5/8"; Clearance Sides=40 5/8"; Cold Water Extension=23 5/8"; Cold Water NPT=2"; Cold Water Radius=1"; Control Panel Extension=29 5/8"; Current=10 A; Drain Extension=26 1/2"; Drain NPT=1"; Drain Radius=1/2"; Energy Extension=27 1/8"; FC OAL=35 3/8"; Flat Side Distance=45 1/4"; Flue Collector Extension=8 1/4"; Flue Diameter=6"; Flue Location=31 1/4"; Flue Radius=3"; Front Skid Extension=68 1/8"; GT Conn Z=58"; GT Z=37 3/8"; Gas Conn X=36 7/8"; Gas Conn Y=13 5/8"; Gas Inlet NPT=1"; Gas Inlet Radius=1/2"; Gas Inlet X=16 7/8"; Gas Inlet Y=3 5/8"; Gas Inlet Z=22 5/8"; Height to Cold Inlet=17 1/16"; Height to Drain=1 7/8"; Height to Energy=28 3/4"; Height to Hot Outlet=68 1/2"; Height to Hot Outlet Actual=68 1/2"; Height to Relief=69 1/8"; Height to Relief Actual=69 1/8"; Hot Outlet Angle=90.00°; Hot Water Extension=23 5/8"; Hot Water NPT=2"; Hot Water Radius=1"; Input Btu/h=600000; Nominal Storage=400 gal; Rear Access Extension=0"; Rear Skid Extension=22 5/8"; Recovery Rate 40F to 140F (gph)=600; Relief Extension=25 5/8"; Size=400; Skid Center Dist=13 1/2"; Skid Length=45 1/2"; Skid Spacing=27"; Unit Height=85 1/2"; Unit Height Actual=85 1/2"; Unit Radius=22 5/8"; Weight=1535
- 2500 L 300A-TP: 500-3000 GIY=5 7/8"; A=13 3/4"; Air Inlet Depth=7"; Air Inlet Diameter=8"; Air Inlet Extension=20 15/16"; Air Inlet Radius=4"; Air Inlet Width=9"; Air Inlet X=15 15/16"; Air Inlet Y=7 3/16"; Air Inlet Y Offset=2 11/16"; Air Inlet Z Offset=5 3/8"; B=4"; Burner Depth=25 15/16"; Burner Height=16 5/8"; Burner Width=22 1/4"; Clearance Front=103 9/16"; Clearance Rear=40 5/8"; Clearance Sides=40 5/8"; Cold Water Extension=23 5/8"; Cold Water NPT=2"; Cold Water Radius=1"; Control Panel Extension=29 5/8"; Current=22 A; Drain Extension=26 1/2"; Drain NPT=1"; Drain Radius=1/2"; Energy Extension=38 1/8"; FC OAL=53 5/8"; Flat Side Distance=45 1/4"; Flue Collector Extension=15 1/2"; Flue Diameter=10"; Flue Location=45 7/8"; Flue Radius=5"; Front Skid Extension=77 5/8"; GT Conn Z=94"; GT Z=55 5/8"; Gas Conn X=44 1/8"; Gas Conn Y=15 7/8"; Gas Inlet NPT=2 1/2"; Gas Inlet Radius=1 1/4"; Gas Inlet X=24 1/8"; Gas Inlet Y=5 7/8"; Gas Inlet Z=40 3/8"; Height to Cold Inlet=17 1/16"; Height to Drain=1 7/8"; Height to Energy=28 3/4"; Height to Hot Outlet=50 7/8"; Height to Hot Outlet Actual=50 7/8"; Height to Relief=57 1/8"; Height to Relief Actual=57 1/8"; Hot Outlet Angle=0.00°; Hot Water Extension=23 5/8"; Hot Water NPT=2"; Hot Water Radius=1"; Input Btu/h=2010000; Nominal Storage=300 gal; Rear Access Extension=-40 5/8"; Rear Skid Extension=22 5/8"; Recovery Rate 40F to 140F (gph)=2000; Relief Extension=25 5/8"; Size=300; Skid Center Dist=13 1/2"; Skid Length=55"; Skid Spacing=27"; Unit Height=73 1/2"; Unit Height Actual=73 1/2"; Unit Radius=22 5/8"; Weight=2205
- 2000 L 300A-TP: 500-3000 GIY=5 1/2"; A=13 3/4"; Air Inlet Depth=7"; Air Inlet Diameter=8"; Air Inlet Extension=20 15/16"; Air Inlet Radius=4"; Air Inlet Width=9"; Air Inlet X=15 15/16"; Air Inlet Y=7 3/16"; Air Inlet Y Offset=2 11/16"; Air Inlet Z Offset=5 3/8"; B=4"; Burner Depth=25 15/16"; Burner Height=16 5/8"; Burner Width=22 1/4"; Clearance Front=103 9/16"; Clearance Rear=40 5/8"; Clearance Sides=40 5/8"; Cold Water Extension=23 5/8"; Cold Water NPT=2"; Cold Water Radius=1"; Control Panel Extension=29 5/8"; Current=22 A; Drain Extension=26 1/2"; Drain NPT=1"; Drain Radius=1/2"; Energy Extension=38 1/8"; FC OAL=53 5/8"; Flat Side Distance=45 1/4"; Flue Collector Extension=15 1/2"; Flue Diameter=10"; Flue Location=45 7/8"; Flue Radius=5"; Front Skid Extension=77 5/8"; GT Conn Z=89 11/16"; GT Z=55 5/8"; Gas Conn X=42"; Gas Conn Y=15 1/2"; Gas Inlet NPT=2"; Gas Inlet Radius=1"; Gas Inlet X=22"; Gas Inlet Y=5 1/2"; Gas Inlet Z=36 1/16"; Height to Cold Inlet=17 1/16"; Height to Drain=1 7/8"; Height to Energy=28 3/4"; Height to Hot Outlet=50 7/8"; Height to Hot Outlet Actual=50 7/8"; Height to Relief=57 1/8"; Height to Relief Actual=57 1/8"; Hot Outlet Angle=0.00°; Hot Water Extension=23 5/8"; Hot Water NPT=2"; Hot Water Radius=1"; Input Btu/h=1600000; Nominal Storage=300 gal; Rear Access Extension=-40 5/8"; Rear Skid Extension=22 5/8"; Recovery Rate 40F to 140F (gph)=1600; Relief Extension=25 5/8"; Size=300; Skid Center Dist=13 1/2"; Skid Length=55"; Skid Spacing=27"; Unit Height=73 1/2"; Unit Height Actual=73 1/2"; Unit Radius=22 5/8"; Weight=2185
- 1500 L 300A-TP: 500-3000 GIY=5 1/2"; A=8 3/8"; Air Inlet Depth=3 1/8"; Air Inlet Diameter=6"; Air Inlet Extension=18 15/16"; Air Inlet Radius=3"; Air Inlet Width=6 3/8"; Air Inlet X=14 7/8"; Air Inlet Y=5 1/4"; Air Inlet Y Offset=2 1/16"; Air Inlet Z Offset=2 1/16"; B=3 15/16"; Burner Depth=15 1/2"; Burner Height=13 3/4"; Burner Width=14 11/16"; Clearance Front=93 1/8"; Clearance Rear=40 5/8"; Clearance Sides=40 5/8"; Cold Water Extension=23 5/8"; Cold Water NPT=2"; Cold Water Radius=1"; Control Panel Extension=29 5/8"; Current=12 A; Drain Extension=26 1/2"; Drain NPT=1"; Drain Radius=1/2"; Energy Extension=38 1/8"; FC OAL=53 5/8"; Flat Side Distance=45 1/4"; Flue Collector Extension=15 1/2"; Flue Diameter=8"; Flue Location=45 7/8"; Flue Radius=4"; Front Skid Extension=77 5/8"; GT Conn Z=90 1/16"; GT Z=55 5/8"; Gas Conn X=40 1/2"; Gas Conn Y=15 1/2"; Gas Inlet NPT=2"; Gas Inlet Radius=1"; Gas Inlet X=20 1/2"; Gas Inlet Y=5 1/2"; Gas Inlet Z=36 7/16"; Height to Cold Inlet=17 1/16"; Height to Drain=1 7/8"; Height to Energy=28 3/4"; Height to Hot Outlet=50 7/8"; Height to Hot Outlet Actual=50 7/8"; Height to Relief=57 1/8"; Height to Relief Actual=57 1/8"; Hot Outlet Angle=0.00°; Hot Water Extension=23 5/8"; Hot Water NPT=2"; Hot Water Radius=1"; Input Btu/h=1200000; Nominal Storage=300 gal; Rear Access Extension=0"; Rear Skid Extension=22 5/8"; Recovery Rate 40F to 140F (gph)=1200; Relief Extension=25 5/8"; Size=300; Skid Center Dist=13 1/2"; Skid Length=55"; Skid Spacing=27"; Unit Height=73 1/2"; Unit Height Actual=73 1/2"; Unit Radius=22 5/8"; Weight=1850
- 1250 L 300A-TP: 500-3000 GIY=5 1/2"; A=8 3/8"; Air Inlet Depth=3 1/8"; Air Inlet Diameter=6"; Air Inlet Extension=18 15/16"; Air Inlet Radius=3"; Air Inlet Width=6 3/8"; Air Inlet X=14 7/8"; Air Inlet Y=5 1/4"; Air Inlet Y Offset=2 1/16"; Air Inlet Z Offset=2 1/16"; B=3 15/16"; Burner Depth=15 1/2"; Burner Height=13 3/4"; Burner Width=14 11/16"; Clearance Front=93 1/8"; Clearance Rear=40 5/8"; Clearance Sides=40 5/8"; Cold Water Extension=23 5/8"; Cold Water NPT=2"; Cold Water Radius=1"; Control Panel Extension=29 5/8"; Current=12 A; Drain Extension=26 1/2"; Drain NPT=1"; Drain Radius=1/2"; Energy Extension=38 1/8"; FC OAL=53 5/8"; Flat Side Distance=45 1/4"; Flue Collector Extension=15 1/2"; Flue Diameter=8"; Flue Location=45 7/8"; Flue Radius=4"; Front Skid Extension=77 5/8"; GT Conn Z=90 1/16"; GT Z=55 5/8"; Gas Conn X=40 1/2"; Gas Conn Y=15 1/2"; Gas Inlet NPT=2"; Gas Inlet Radius=1"; Gas Inlet X=20 1/2"; Gas Inlet Y=5 1/2"; Gas Inlet Z=36 7/16"; Height to Cold Inlet=17 1/16"; Height to Drain=1 7/8"; Height to Energy=28 3/4"; Height to Hot Outlet=50 7/8"; Height to Hot Outlet Actual=50 7/8"; Height to Relief=57 1/8"; Height to Relief Actual=57 1/8"; Hot Outlet Angle=0.00°; Hot Water Extension=23 5/8"; Hot Water NPT=2"; Hot Water Radius=1"; Input Btu/h=1000000; Nominal Storage=300 gal; Rear Access Extension=0"; Rear Skid Extension=22 5/8"; Recovery Rate 40F to 140F (gph)=1000; Relief Extension=25 5/8"; Size=300; Skid Center Dist=13 1/2"; Skid Length=55"; Skid Spacing=27"; Unit Height=73 1/2"; Unit Height Actual=73 1/2"; Unit Radius=22 5/8"; Weight=1765
- 1000 L 300A-TP: 500-3000 GIY=4 1/2"; A=8 3/8"; Air Inlet Depth=3 1/8"; Air Inlet Diameter=6"; Air Inlet Extension=18 15/16"; Air Inlet Radius=3"; Air Inlet Width=6 3/8"; Air Inlet X=14 7/8"; Air Inlet Y=5 1/4"; Air Inlet Y Offset=2 1/16"; Air Inlet Z Offset=2 1/16"; B=3 15/16"; Burner Depth=15 1/2"; Burner Height=13 3/4"; Burner Width=14 11/16"; Clearance Front=74 7/8"; Clearance Rear=40 5/8"; Clearance Sides=40 5/8"; Cold Water Extension=23 5/8"; Cold Water NPT=2"; Cold Water Radius=1"; Control Panel Extension=29 5/8"; Current=10 A; Drain Extension=26 1/2"; Drain NPT=1"; Drain Radius=1/2"; Energy Extension=27 1/8"; FC OAL=35 3/8"; Flat Side Distance=45 1/4"; Flue Collector Extension=8 1/4"; Flue Diameter=8"; Flue Location=31 1/4"; Flue Radius=4"; Front Skid Extension=68 1/8"; GT Conn Z=63 1/16"; GT Z=37 3/8"; Gas Conn X=40 1/2"; Gas Conn Y=14 1/2"; Gas Inlet NPT=1 1/4"; Gas Inlet Radius=5/8"; Gas Inlet X=20 1/2"; Gas Inlet Y=4 1/2"; Gas Inlet Z=27 11/16"; Height to Cold Inlet=17 1/16"; Height to Drain=1 7/8"; Height to Energy=28 3/4"; Height to Hot Outlet=50 7/8"; Height to Hot Outlet Actual=50 7/8"; Height to Relief=57 1/8"; Height to Relief Actual=57 1/8"; Hot Outlet Angle=0.00°; Hot Water Extension=23 5/8"; Hot Water NPT=2"; Hot Water Radius=1"; Input Btu/h=800000; Nominal Storage=300 gal; Rear Access Extension=0"; Rear Skid Extension=22 5/8"; Recovery Rate 40F to 140F (gph)=800; Relief Extension=25 5/8"; Size=300; Skid Center Dist=13 1/2"; Skid Length=45 1/2"; Skid Spacing=27"; Unit Height=73 1/2"; Unit Height Actual=73 1/2"; Unit Radius=22 5/8"; Weight=1530
- 750 L 300A-TP: 500-3000 GIY=3 5/8"; A=8 3/8"; Air Inlet Depth=3 1/8"; Air Inlet Diameter=6"; Air Inlet Extension=18 15/16"; Air Inlet Radius=3"; Air Inlet Width=6 3/8"; Air Inlet X=14 7/8"; Air Inlet Y=5 1/4"; Air Inlet Y Offset=2 1/16"; Air Inlet Z Offset=2 1/16"; B=3 15/16"; Burner Depth=15 1/2"; Burner Height=13 3/4"; Burner Width=14 11/16"; Clearance Front=74 7/8"; Clearance Rear=40 5/8"; Clearance Sides=40 5/8"; Cold Water Extension=23 5/8"; Cold Water NPT=2"; Cold Water Radius=1"; Control Panel Extension=29 5/8"; Current=10 A; Drain Extension=26 1/2"; Drain NPT=1"; Drain Radius=1/2"; Energy Extension=27 1/8"; FC OAL=35 3/8"; Flat Side Distance=45 1/4"; Flue Collector Extension=8 1/4"; Flue Diameter=6"; Flue Location=31 1/4"; Flue Radius=3"; Front Skid Extension=68 1/8"; GT Conn Z=58"; GT Z=37 3/8"; Gas Conn X=36 7/8"; Gas Conn Y=13 5/8"; Gas Inlet NPT=1"; Gas Inlet Radius=1/2"; Gas Inlet X=16 7/8"; Gas Inlet Y=3 5/8"; Gas Inlet Z=22 5/8"; Height to Cold Inlet=17 1/16"; Height to Drain=1 7/8"; Height to Energy=28 3/4"; Height to Hot Outlet=50 7/8"; Height to Hot Outlet Actual=50 7/8"; Height to Relief=57 1/8"; Height to Relief Actual=57 1/8"; Hot Outlet Angle=0.00°; Hot Water Extension=23 5/8"; Hot Water NPT=2"; Hot Water Radius=1"; Input Btu/h=600000; Nominal Storage=300 gal; Rear Access Extension=0"; Rear Skid Extension=22 5/8"; Recovery Rate 40F to 140F (gph)=600; Relief Extension=25 5/8"; Size=300; Skid Center Dist=13 1/2"; Skid Length=45 1/2"; Skid Spacing=27"; Unit Height=73 1/2"; Unit Height Actual=73 1/2"; Unit Radius=22 5/8"; Weight=1490
- 1500 L 250A-TP: 500-3000 GIY=5 1/2"; A=8 3/8"; Air Inlet Depth=3 1/8"; Air Inlet Diameter=6"; Air Inlet Extension=18 15/16"; Air Inlet Radius=3"; Air Inlet Width=6 3/8"; Air Inlet X=14 7/8"; Air Inlet Y=5 1/4"; Air Inlet Y Offset=2 1/16"; Air Inlet Z Offset=2 1/16"; B=3 15/16"; Burner Depth=15 1/2"; Burner Height=13 3/4"; Burner Width=14 11/16"; Clearance Front=93 1/8"; Clearance Rear=40 5/8"; Clearance Sides=40 5/8"; Cold Water Extension=23 5/8"; Cold Water NPT=2"; Cold Water Radius=1"; Control Panel Extension=29 5/8"; Current=12 A; Drain Extension=26 1/2"; Drain NPT=1"; Drain Radius=1/2"; Energy Extension=38 1/8"; FC OAL=53 5/8"; Flat Side Distance=45 1/4"; Flue Collector Extension=15 1/2"; Flue Diameter=8"; Flue Location=45 7/8"; Flue Radius=4"; Front Skid Extension=77 5/8"; GT Conn Z=90 1/16"; GT Z=55 5/8"; Gas Conn X=40 1/2"; Gas Conn Y=15 1/2"; Gas Inlet NPT=2"; Gas Inlet Radius=1"; Gas Inlet X=20 1/2"; Gas Inlet Y=5 1/2"; Gas Inlet Z=36 7/16"; Height to Cold Inlet=17 1/16"; Height to Drain=1 7/8"; Height to Energy=28 3/4"; Height to Hot Outlet=38 7/8"; Height to Hot Outlet Actual=38 7/8"; Height to Relief=45 1/8"; Height to Relief Actual=45 1/8"; Hot Outlet Angle=0.00°; Hot Water Extension=23 5/8"; Hot Water NPT=2"; Hot Water Radius=1"; Input Btu/h=1200000; Nominal Storage=250 gal; Rear Access Extension=0"; Rear Skid Extension=22 5/8"; Recovery Rate 40F to 140F (gph)=1200; Relief Extension=25 5/8"; Size=250; Skid Center Dist=13 1/2"; Skid Length=55"; Skid Spacing=27"; Unit Height=61 1/2"; Unit Height Actual=61 1/2"; Unit Radius=22 5/8"; Weight=1710
- 1250 L 250A-TP: 500-3000 GIY=5 1/2"; A=8 3/8"; Air Inlet Depth=3 1/8"; Air Inlet Diameter=6"; Air Inlet Extension=18 15/16"; Air Inlet Radius=3"; Air Inlet Width=6 3/8"; Air Inlet X=14 7/8"; Air Inlet Y=5 1/4"; Air Inlet Y Offset=2 1/16"; Air Inlet Z Offset=2 1/16"; B=3 15/16"; Burner Depth=15 1/2"; Burner Height=13 3/4"; Burner Width=14 11/16"; Clearance Front=93 1/8"; Clearance Rear=40 5/8"; Clearance Sides=40 5/8"; Cold Water Extension=23 5/8"; Cold Water NPT=2"; Cold Water Radius=1"; Control Panel Extension=29 5/8"; Current=12 A; Drain Extension=26 1/2"; Drain NPT=1"; Drain Radius=1/2"; Energy Extension=38 1/8"; FC OAL=53 5/8"; Flat Side Distance=45 1/4"; Flue Collector Extension=15 1/2"; Flue Diameter=8"; Flue Location=45 7/8"; Flue Radius=4"; Front Skid Extension=77 5/8"; GT Conn Z=90 1/16"; GT Z=55 5/8"; Gas Conn X=40 1/2"; Gas Conn Y=15 1/2"; Gas Inlet NPT=2"; Gas Inlet Radius=1"; Gas Inlet X=20 1/2"; Gas Inlet Y=5 1/2"; Gas Inlet Z=36 7/16"; Height to Cold Inlet=17 1/16"; Height to Drain=1 7/8"; Height to Energy=28 3/4"; Height to Hot Outlet=38 7/8"; Height to Hot Outlet Actual=38 7/8"; Height to Relief=45 1/8"; Height to Relief Actual=45 1/8"; Hot Outlet Angle=0.00°; Hot Water Extension=23 5/8"; Hot Water NPT=2"; Hot Water Radius=1"; Input Btu/h=1000000; Nominal Storage=250 gal; Rear Access Extension=0"; Rear Skid Extension=22 5/8"; Recovery Rate 40F to 140F (gph)=1000; Relief Extension=25 5/8"; Size=250; Skid Center Dist=13 1/2"; Skid Length=55"; Skid Spacing=27"; Unit Height=61 1/2"; Unit Height Actual=61 1/2"; Unit Radius=22 5/8"; Weight=1700
- 1000 L 250A-TP: 500-3000 GIY=4 1/2"; A=8 3/8"; Air Inlet Depth=3 1/8"; Air Inlet Diameter=6"; Air Inlet Extension=18 15/16"; Air Inlet Radius=3"; Air Inlet Width=6 3/8"; Air Inlet X=14 7/8"; Air Inlet Y=5 1/4"; Air Inlet Y Offset=2 1/16"; Air Inlet Z Offset=2 1/16"; B=3 15/16"; Burner Depth=15 1/2"; Burner Height=13 3/4"; Burner Width=14 11/16"; Clearance Front=74 7/8"; Clearance Rear=40 5/8"; Clearance Sides=40 5/8"; Cold Water Extension=23 5/8"; Cold Water NPT=2"; Cold Water Radius=1"; Control Panel Extension=29 5/8"; Current=10 A; Drain Extension=26 1/2"; Drain NPT=1"; Drain Radius=1/2"; Energy Extension=27 1/8"; FC OAL=35 3/8"; Flat Side Distance=45 1/4"; Flue Collector Extension=8 1/4"; Flue Diameter=8"; Flue Location=31 1/4"; Flue Radius=4"; Front Skid Extension=68 1/8"; GT Conn Z=63 1/16"; GT Z=37 3/8"; Gas Conn X=40 1/2"; Gas Conn Y=14 1/2"; Gas Inlet NPT=1 1/4"; Gas Inlet Radius=5/8"; Gas Inlet X=20 1/2"; Gas Inlet Y=4 1/2"; Gas Inlet Z=27 11/16"; Height to Cold Inlet=17 1/16"; Height to Drain=1 7/8"; Height to Energy=28 3/4"; Height to Hot Outlet=38 7/8"; Height to Hot Outlet Actual=38 7/8"; Height to Relief=45 1/8"; Height to Relief Actual=45 1/8"; Hot Outlet Angle=0.00°; Hot Water Extension=23 5/8"; Hot Water NPT=2"; Hot Water Radius=1"; Input Btu/h=800000; Nominal Storage=250 gal; Rear Access Extension=0"; Rear Skid Extension=22 5/8"; Recovery Rate 40F to 140F (gph)=800; Relief Extension=25 5/8"; Size=250; Skid Center Dist=13 1/2"; Skid Length=45 1/2"; Skid Spacing=27"; Unit Height=61 1/2"; Unit Height Actual=61 1/2"; Unit Radius=22 5/8"; Weight=1470
- 750 L 250A-TP: 500-3000 GIY=3 5/8"; A=8 3/8"; Air Inlet Depth=3 1/8"; Air Inlet Diameter=6"; Air Inlet Extension=18 15/16"; Air Inlet Radius=3"; Air Inlet Width=6 3/8"; Air Inlet X=14 7/8"; Air Inlet Y=5 1/4"; Air Inlet Y Offset=2 1/16"; Air Inlet Z Offset=2 1/16"; B=3 15/16"; Burner Depth=15 1/2"; Burner Height=13 3/4"; Burner Width=14 11/16"; Clearance Front=74 7/8"; Clearance Rear=40 5/8"; Clearance Sides=40 5/8"; Cold Water Extension=23 5/8"; Cold Water NPT=2"; Cold Water Radius=1"; Control Panel Extension=29 5/8"; Current=10 A; Drain Extension=26 1/2"; Drain NPT=1"; Drain Radius=1/2"; Energy Extension=27 1/8"; FC OAL=35 3/8"; Flat Side Distance=45 1/4"; Flue Collector Extension=8 1/4"; Flue Diameter=6"; Flue Location=31 1/4"; Flue Radius=3"; Front Skid Extension=68 1/8"; GT Conn Z=58"; GT Z=37 3/8"; Gas Conn X=36 7/8"; Gas Conn Y=13 5/8"; Gas Inlet NPT=1"; Gas Inlet Radius=1/2"; Gas Inlet X=16 7/8"; Gas Inlet Y=3 5/8"; Gas Inlet Z=22 5/8"; Height to Cold Inlet=17 1/16"; Height to Drain=1 7/8"; Height to Energy=28 3/4"; Height to Hot Outlet=38 7/8"; Height to Hot Outlet Actual=38 7/8"; Height to Relief=45 1/8"; Height to Relief Actual=45 1/8"; Hot Outlet Angle=0.00°; Hot Water Extension=23 5/8"; Hot Water NPT=2"; Hot Water Radius=1"; Input Btu/h=600000; Nominal Storage=250 gal; Rear Access Extension=0"; Rear Skid Extension=22 5/8"; Recovery Rate 40F to 140F (gph)=600; Relief Extension=25 5/8"; Size=250; Skid Center Dist=13 1/2"; Skid Length=45 1/2"; Skid Spacing=27"; Unit Height=61 1/2"; Unit Height Actual=61 1/2"; Unit Radius=22 5/8"; Weight=1430
- 1000 L 215A-TP: 500-3000 GIY=4 1/2"; A=8 3/8"; Air Inlet Depth=3 1/8"; Air Inlet Diameter=6"; Air Inlet Extension=18 15/16"; Air Inlet Radius=3"; Air Inlet Width=6 3/8"; Air Inlet X=14 7/8"; Air Inlet Y=5 1/4"; Air Inlet Y Offset=2 1/16"; Air Inlet Z Offset=2 1/16"; B=3 15/16"; Burner Depth=15 1/2"; Burner Height=13 3/4"; Burner Width=14 11/16"; Clearance Front=84 7/8"; Clearance Rear=36 1/8"; Clearance Sides=36 1/8"; Cold Water Extension=19 1/8"; Cold Water NPT=2"; Cold Water Radius=1"; Control Panel Extension=25 1/8"; Current=10 A; Drain Extension=22"; Drain NPT=1"; Drain Radius=1/2"; Energy Extension=37 1/8"; FC OAL=45 3/8"; Flat Side Distance=34"; Flue Collector Extension=8 1/4"; Flue Diameter=8"; Flue Location=41 1/4"; Flue Radius=4"; Front Skid Extension=54 3/8"; GT Conn Z=73 1/16"; GT Z=47 3/8"; Gas Conn X=40 1/2"; Gas Conn Y=14 1/2"; Gas Inlet NPT=1 1/4"; Gas Inlet Radius=5/8"; Gas Inlet X=20 1/2"; Gas Inlet Y=4 1/2"; Gas Inlet Z=27 11/16"; Height to Cold Inlet=14 13/16"; Height to Drain=1 7/8"; Height to Energy=26 1/2"; Height to Hot Outlet=64 1/2"; Height to Hot Outlet Actual=64 1/2"; Height to Relief=64 7/8"; Height to Relief Actual=64 7/8"; Hot Outlet Angle=90.00°; Hot Water Extension=19 1/8"; Hot Water NPT=2"; Hot Water Radius=1"; Input Btu/h=800000; Nominal Storage=215 gal; Rear Access Extension=0"; Rear Skid Extension=18 1/8"; Recovery Rate 40F to 140F (gph)=800; Relief Extension=21 1/8"; Size=215; Skid Center Dist=8 1/2"; Skid Length=36 1/4"; Skid Spacing=17"; Unit Height=76 1/2"; Unit Height Actual=76 1/2"; Unit Radius=18 1/8"; Weight=1425
- 750 L 215A-TP: 500-3000 GIY=3 5/8"; A=8 3/8"; Air Inlet Depth=3 1/8"; Air Inlet Diameter=6"; Air Inlet Extension=18 15/16"; Air Inlet Radius=3"; Air Inlet Width=6 3/8"; Air Inlet X=14 7/8"; Air Inlet Y=5 1/4"; Air Inlet Y Offset=2 1/16"; Air Inlet Z Offset=2 1/16"; B=3 15/16"; Burner Depth=15 1/2"; Burner Height=13 3/4"; Burner Width=14 11/16"; Clearance Front=84 7/8"; Clearance Rear=36 1/8"; Clearance Sides=36 1/8"; Cold Water Extension=19 1/8"; Cold Water NPT=2"; Cold Water Radius=1"; Control Panel Extension=25 1/8"; Current=10 A; Drain Extension=22"; Drain NPT=1"; Drain Radius=1/2"; Energy Extension=37 1/8"; FC OAL=45 3/8"; Flat Side Distance=34"; Flue Collector Extension=8 1/4"; Flue Diameter=6"; Flue Location=41 1/4"; Flue Radius=3"; Front Skid Extension=54 3/8"; GT Conn Z=68"; GT Z=47 3/8"; Gas Conn X=36 7/8"; Gas Conn Y=13 5/8"; Gas Inlet NPT=1"; Gas Inlet Radius=1/2"; Gas Inlet X=16 7/8"; Gas Inlet Y=3 5/8"; Gas Inlet Z=22 5/8"; Height to Cold Inlet=14 13/16"; Height to Drain=1 7/8"; Height to Energy=26 1/2"; Height to Hot Outlet=64 1/2"; Height to Hot Outlet Actual=64 1/2"; Height to Relief=64 7/8"; Height to Relief Actual=64 7/8"; Hot Outlet Angle=90.00°; Hot Water Extension=19 1/8"; Hot Water NPT=2"; Hot Water Radius=1"; Input Btu/h=600000; Nominal Storage=215 gal; Rear Access Extension=0"; Rear Skid Extension=18 1/8"; Recovery Rate 40F to 140F (gph)=600; Relief Extension=21 1/8"; Size=215; Skid Center Dist=8 1/2"; Skid Length=36 1/4"; Skid Spacing=17"; Unit Height=76 1/2"; Unit Height Actual=76 1/2"; Unit Radius=18 1/8"; Weight=1370
- 1000 L 175A-TP: 500-3000 GIY=4 1/2"; A=8 3/8"; Air Inlet Depth=3 1/8"; Air Inlet Diameter=6"; Air Inlet Extension=18 15/16"; Air Inlet Radius=3"; Air Inlet Width=6 3/8"; Air Inlet X=14 7/8"; Air Inlet Y=5 1/4"; Air Inlet Y Offset=2 1/16"; Air Inlet Z Offset=2 1/16"; B=3 15/16"; Burner Depth=15 1/2"; Burner Height=13 3/4"; Burner Width=14 11/16"; Clearance Front=84 7/8"; Clearance Rear=36 1/8"; Clearance Sides=36 1/8"; Cold Water Extension=19 1/8"; Cold Water NPT=2"; Cold Water Radius=1"; Control Panel Extension=25 1/8"; Current=10 A; Drain Extension=22"; Drain NPT=1"; Drain Radius=1/2"; Energy Extension=37 1/8"; FC OAL=45 3/8"; Flat Side Distance=34"; Flue Collector Extension=8 1/4"; Flue Diameter=8"; Flue Location=41 1/4"; Flue Radius=4"; Front Skid Extension=54 3/8"; GT Conn Z=73 1/16"; GT Z=47 3/8"; Gas Conn X=40 1/2"; Gas Conn Y=14 1/2"; Gas Inlet NPT=1 1/4"; Gas Inlet Radius=5/8"; Gas Inlet X=20 1/2"; Gas Inlet Y=4 1/2"; Gas Inlet Z=27 11/16"; Height to Cold Inlet=14 13/16"; Height to Drain=1 7/8"; Height to Energy=26 1/2"; Height to Hot Outlet=50 7/8"; Height to Hot Outlet Actual=50 7/8"; Height to Relief=57 7/8"; Height to Relief Actual=57 7/8"; Hot Outlet Angle=0.00°; Hot Water Extension=19 1/8"; Hot Water NPT=2"; Hot Water Radius=1"; Input Btu/h=800000; Nominal Storage=175 gal; Rear Access Extension=0"; Rear Skid Extension=18 1/8"; Recovery Rate 40F to 140F (gph)=800; Relief Extension=21 1/8"; Size=175; Skid Center Dist=8 1/2"; Skid Length=36 1/4"; Skid Spacing=17"; Unit Height=69 1/2"; Unit Height Actual=69 1/2"; Unit Radius=18 1/8"; Weight=1430
- 750 L 175A-TP: 500-3000 GIY=3 5/8"; A=8 3/8"; Air Inlet Depth=3 1/8"; Air Inlet Diameter=6"; Air Inlet Extension=18 15/16"; Air Inlet Radius=3"; Air Inlet Width=6 3/8"; Air Inlet X=14 7/8"; Air Inlet Y=5 1/4"; Air Inlet Y Offset=2 1/16"; Air Inlet Z Offset=2 1/16"; B=3 15/16"; Burner Depth=15 1/2"; Burner Height=13 3/4"; Burner Width=14 11/16"; Clearance Front=84 7/8"; Clearance Rear=36 1/8"; Clearance Sides=36 1/8"; Cold Water Extension=19 1/8"; Cold Water NPT=2"; Cold Water Radius=1"; Control Panel Extension=25 1/8"; Current=10 A; Drain Extension=22"; Drain NPT=1"; Drain Radius=1/2"; Energy Extension=37 1/8"; FC OAL=45 3/8"; Flat Side Distance=34"; Flue Collector Extension=8 1/4"; Flue Diameter=6"; Flue Location=41 1/4"; Flue Radius=3"; Front Skid Extension=54 3/8"; GT Conn Z=68"; GT Z=47 3/8"; Gas Conn X=36 7/8"; Gas Conn Y=13 5/8"; Gas Inlet NPT=1"; Gas Inlet Radius=1/2"; Gas Inlet X=16 7/8"; Gas Inlet Y=3 5/8"; Gas Inlet Z=22 5/8"; Height to Cold Inlet=14 13/16"; Height to Drain=1 7/8"; Height to Energy=26 1/2"; Height to Hot Outlet=50 7/8"; Height to Hot Outlet Actual=50 7/8"; Height to Relief=57 7/8"; Height to Relief Actual=57 7/8"; Hot Outlet Angle=0.00°; Hot Water Extension=19 1/8"; Hot Water NPT=2"; Hot Water Radius=1"; Input Btu/h=600000; Nominal Storage=175 gal; Rear Access Extension=0"; Rear Skid Extension=18 1/8"; Recovery Rate 40F to 140F (gph)=600; Relief Extension=21 1/8"; Size=175; Skid Center Dist=8 1/2"; Skid Length=36 1/4"; Skid Spacing=17"; Unit Height=69 1/2"; Unit Height Actual=69 1/2"; Unit Radius=18 1/8"; Weight=1220
- 1000 L 150A-TP: 500-3000 GIY=4 1/2"; A=8 3/8"; Air Inlet Depth=3 1/8"; Air Inlet Diameter=6"; Air Inlet Extension=18 15/16"; Air Inlet Radius=3"; Air Inlet Width=6 3/8"; Air Inlet X=14 7/8"; Air Inlet Y=5 1/4"; Air Inlet Y Offset=2 1/16"; Air Inlet Z Offset=2 1/16"; B=3 15/16"; Burner Depth=15 1/2"; Burner Height=13 3/4"; Burner Width=14 11/16"; Clearance Front=84 7/8"; Clearance Rear=36 1/8"; Clearance Sides=36 1/8"; Cold Water Extension=19 1/8"; Cold Water NPT=2"; Cold Water Radius=1"; Control Panel Extension=25 1/8"; Current=10 A; Drain Extension=22"; Drain NPT=1"; Drain Radius=1/2"; Energy Extension=37 1/8"; FC OAL=45 3/8"; Flat Side Distance=34"; Flue Collector Extension=8 1/4"; Flue Diameter=8"; Flue Location=41 1/4"; Flue Radius=4"; Front Skid Extension=54 3/8"; GT Conn Z=73 1/16"; GT Z=47 3/8"; Gas Conn X=40 1/2"; Gas Conn Y=14 1/2"; Gas Inlet NPT=1 1/4"; Gas Inlet Radius=5/8"; Gas Inlet X=20 1/2"; Gas Inlet Y=4 1/2"; Gas Inlet Z=27 11/16"; Height to Cold Inlet=14 13/16"; Height to Drain=1 7/8"; Height to Energy=26 1/2"; Height to Hot Outlet=44 7/8"; Height to Hot Outlet Actual=44 7/8"; Height to Relief=51 7/8"; Height to Relief Actual=51 7/8"; Hot Outlet Angle=0.00°; Hot Water Extension=19 1/8"; Hot Water NPT=2"; Hot Water Radius=1"; Input Btu/h=800000; Nominal Storage=150 gal; Rear Access Extension=0"; Rear Skid Extension=18 1/8"; Recovery Rate 40F to 140F (gph)=800; Relief Extension=21 1/8"; Size=150; Skid Center Dist=8 1/2"; Skid Length=36 1/4"; Skid Spacing=17"; Unit Height=63 1/2"; Unit Height Actual=63 1/2"; Unit Radius=18 1/8"; Weight=1365
- 750 L 150A-TP: 500-3000 GIY=3 5/8"; A=8 3/8"; Air Inlet Depth=3 1/8"; Air Inlet Diameter=6"; Air Inlet Extension=18 15/16"; Air Inlet Radius=3"; Air Inlet Width=6 3/8"; Air Inlet X=14 7/8"; Air Inlet Y=5 1/4"; Air Inlet Y Offset=2 1/16"; Air Inlet Z Offset=2 1/16"; B=3 15/16"; Burner Depth=15 1/2"; Burner Height=13 3/4"; Burner Width=14 11/16"; Clearance Front=84 7/8"; Clearance Rear=36 1/8"; Clearance Sides=36 1/8"; Cold Water Extension=19 1/8"; Cold Water NPT=2"; Cold Water Radius=1"; Control Panel Extension=25 1/8"; Current=10 A; Drain Extension=22"; Drain NPT=1"; Drain Radius=1/2"; Energy Extension=37 1/8"; FC OAL=45 3/8"; Flat Side Distance=34"; Flue Collector Extension=8 1/4"; Flue Diameter=6"; Flue Location=41 1/4"; Flue Radius=3"; Front Skid Extension=54 3/8"; GT Conn Z=68"; GT Z=47 3/8"; Gas Conn X=36 7/8"; Gas Conn Y=13 5/8"; Gas Inlet NPT=1"; Gas Inlet Radius=1/2"; Gas Inlet X=16 7/8"; Gas Inlet Y=3 5/8"; Gas Inlet Z=22 5/8"; Height to Cold Inlet=14 13/16"; Height to Drain=1 7/8"; Height to Energy=26 1/2"; Height to Hot Outlet=44 7/8"; Height to Hot Outlet Actual=44 7/8"; Height to Relief=51 7/8"; Height to Relief Actual=51 7/8"; Hot Outlet Angle=0.00°; Hot Water Extension=19 1/8"; Hot Water NPT=2"; Hot Water Radius=1"; Input Btu/h=600000; Nominal Storage=150 gal; Rear Access Extension=0"; Rear Skid Extension=18 1/8"; Recovery Rate 40F to 140F (gph)=600; Relief Extension=21 1/8"; Size=150; Skid Center Dist=8 1/2"; Skid Length=36 1/4"; Skid Spacing=17"; Unit Height=63 1/2"; Unit Height Actual=63 1/2"; Unit Radius=18 1/8"; Weight=1155

note: column(s) folded — value = type name in every type: Model

## geometry (parser evidence)
native form markers: Blend x2, Sweep x3
no freeform markers — native parametric forms only
